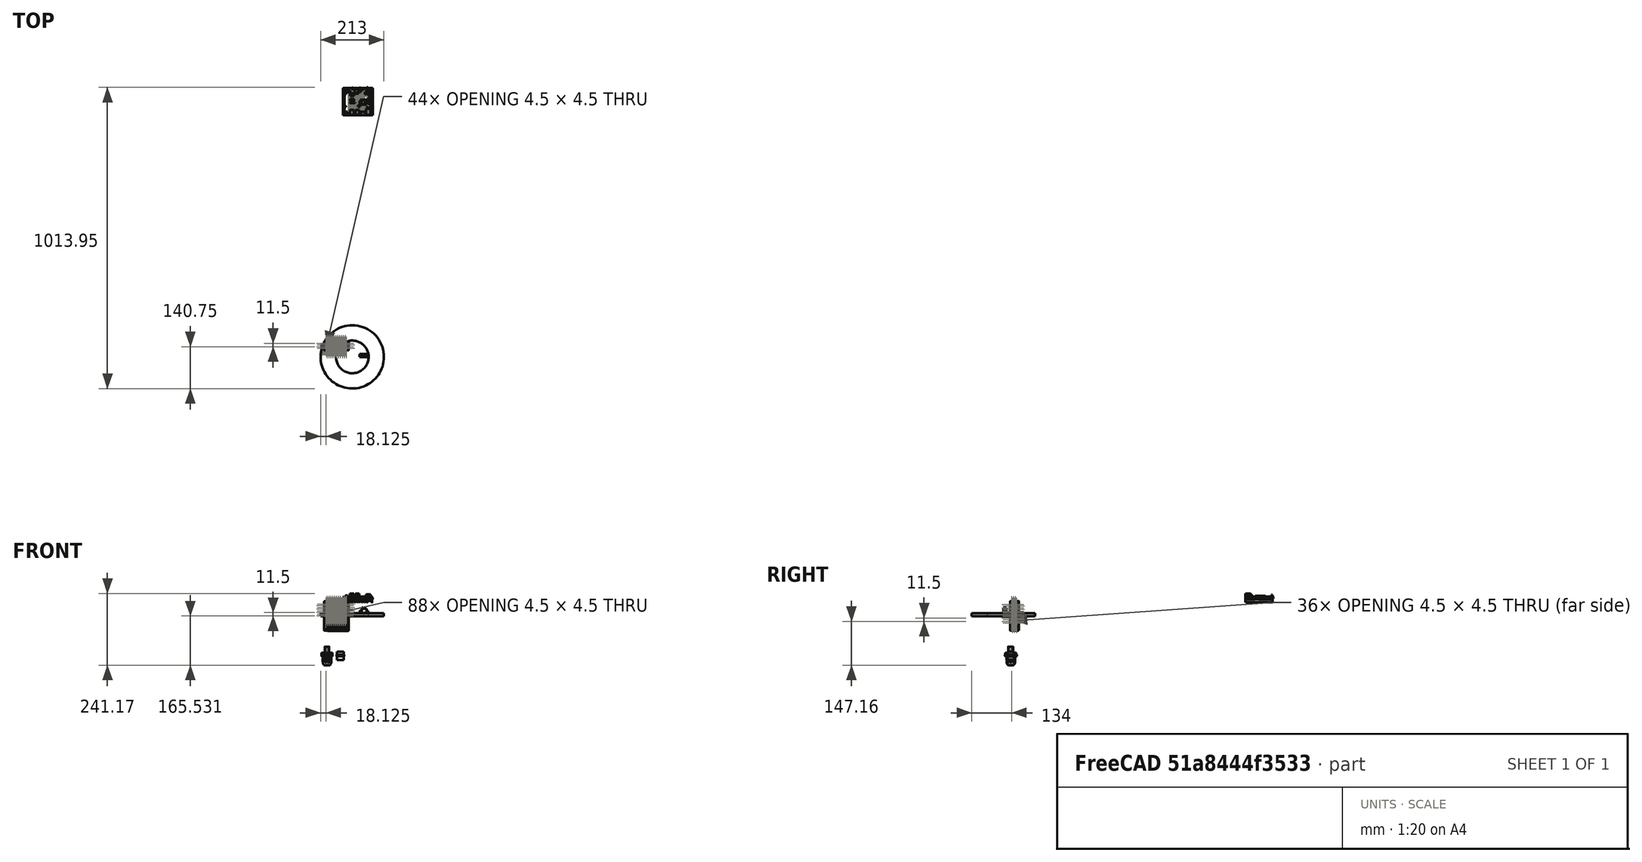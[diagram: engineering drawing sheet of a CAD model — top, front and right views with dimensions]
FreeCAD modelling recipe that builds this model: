
FCSTD DOCUMENT  (FreeCAD 0.20R29410 (Git))
Label: lightSensingModule
License: All rights reserved
LicenseURL: http://en.wikipedia.org/wiki/All_rights_reserved
objects: Part::Feature×21, Part::Cylinder×3, Sketcher::SketchObject×2, Part::Extrusion×2, App::Part×1, Part::MultiFuse×1, Mesh::Feature×1
note: 29 computed .brp shape members not serialized (recipe doc carries the construction recipe); baked Part::Feature solids carry a one-line shape summary decoded from their .brp

FEATURE [Part::Cylinder] Cylinder  label="lens"
  Angle = 360
  AttacherType = Attacher::AttachEngine3D
  FirstAngle = 0
  Height = 10
  Radius = 106.5
  SecondAngle = 0
FEATURE [Part::Cylinder] Cylinder001  label="lens001"
  Angle = 360
  AttacherType = Attacher::AttachEngine3D
  FirstAngle = 0
  Height = 10
  Radius = 55
  SecondAngle = 0
FEATURE [Part::Feature] Part__Feature025  label="CUI_VGS-35C-12"
  Placement = pos=(-55,36,1) rot=(1,0,0;3.14159rad)
  shape: bbox 82.03 x 30.06 x 100 mm, 2215 faces, 10 solids (baked)
FEATURE [Part::Feature] Part__Feature007  label="Heat Sink"
  shape: bbox 100 x 91 x 19 mm, 161 faces (baked)
FEATURE [Part::Feature] Part__Feature008  label="Battery Holder"
  shape: bbox 28.5 x 16 x 6 mm, 91 faces (baked)
FEATURE [Part::Feature] Part__Feature009  label="DC Jack"
  shape: bbox 7.6 x 11.5 x 9.75 mm, 10 faces (baked)
FEATURE [Part::Feature] Part__Feature010  label="PCB"
  shape: bbox 90 x 90 x 3.3 mm, 59 faces (baked)
FEATURE [Part::Feature] Part__Feature011  label="HDMI"
  shape: bbox 14.51 x 11.61 x 5.506 mm, 31 faces (baked)
FEATURE [Part::Feature] Part__Feature012  label="Ethernet"
  shape: bbox 15.9 x 21.4 x 13.5 mm, 25 faces (baked)
FEATURE [Part::Feature] Part__Feature013  label="USB 3.0 B"
  shape: bbox 14.55 x 17.5 x 16.15 mm, 36 faces (baked)
FEATURE [Part::Feature] Part__Feature014  label="USB 3.0 A"
  shape: bbox 14.55 x 17.5 x 16.15 mm, 36 faces (baked)
FEATURE [Part::Feature] Part__Feature015  label="Audio Jack"
  shape: bbox 6.5 x 14 x 4 mm, 10 faces (baked)
FEATURE [Part::Feature] Part__Feature016  label="Fan Plug"
  shape: bbox 3.75 x 7.5 x 4.75 mm, 32 faces (baked)
FEATURE [Part::Feature] Part__Feature017  label="REMOCON"
  shape: bbox 7.006 x 5.006 x 12.01 mm, 30 faces (baked)
FEATURE [Part::Feature] Part__Feature018  label="eMMC"
  shape: bbox 13.5 x 18.5 x 2.8 mm, 33 faces (baked)
FEATURE [Part::Feature] Part__Feature019  label="MicroUSB"
  shape: bbox 7.012 x 4.616 x 3.511 mm, 31 faces (baked)
FEATURE [Part::Feature] Part__Feature020  label="Switch"
  shape: bbox 9 x 5.74 x 3.5 mm, 11 faces (baked)
FEATURE [Part::Feature] Part__Feature021  label="MicroSD Card Socket"
  shape: bbox 11.5 x 5.5 x 3.5 mm, 11 faces (baked)
FEATURE [Part::Feature] Part__Feature022  label="7 Pin Header"
  shape: bbox 17.5 x 2.5 x 8 mm, 41 faces (baked)
FEATURE [Part::Feature] Part__Feature023  label="UART"
  shape: bbox 5 x 12.5 x 6 mm, 43 faces (baked)
FEATURE [Part::Feature] Part__Feature024  label="40 Pin Header"
  shape: bbox 5 x 50 x 8 mm, 206 faces (baked)
FEATURE [App::Part] Odroid_N2__v4  label="Odroid-N2+ v4"
  Group = -> [Part__Feature007,Part__Feature008,Part__Feature009,Part__Feature010,Part__Feature011,Part__Feature012,Part__Feature013,Part__Feature014,Part__Feature015,Part__Feature016,Part__Feature017,Part__Feature018,Part__Feature019,Part__Feature020,Part__Feature021,Part__Feature022,Part__Feature023,Part__Feature024]
  Origin = -> Origin002
  Placement = pos=(31,-814,-44.46) rot=(0,0,1;0rad)
FEATURE [Part::Cylinder] Cylinder002  label="plugIn"
  Angle = 360
  AttacherType = Attacher::AttachEngine3D
  FirstAngle = 0
  Height = 28.19
  Radius = 11
  SecondAngle = 0
FEATURE [Part::Feature] Part__Feature027  label="DCC-RJ6ST-310"
  Placement = pos=(-85,25,-123) rot=(0,0,1;0rad)
  shape: bbox 40.36 x 68.07 x 51.72 mm, 441 faces (baked)
FEATURE [Part::Feature] Part__Feature028  label="DCP-RJ6ST-F"
  Placement = pos=(-85,25,-123.5) rot=(0,1,0;3.14159rad)
  shape: bbox 40.26 x 40.33 x 38.85 mm, 485 faces, 2 solids (baked)
FEATURE [Sketcher::SketchObject] Sketch
  FullyConstrained = true
  sketch-geometry (7):
    g0: LineSegment StartX=12.25 StartY=-7.07254 StartZ=0 EndX=12.25 EndY=7.07254 EndZ=0
    g1: LineSegment StartX=12.25 StartY=7.07254 StartZ=0 EndX=0 EndY=14.1451 EndZ=0
    g2: LineSegment StartX=0 StartY=14.1451 StartZ=0 EndX=-12.25 EndY=7.07254 EndZ=0
    g3: LineSegment StartX=-12.25 StartY=7.07254 StartZ=0 EndX=-12.25 EndY=-7.07254 EndZ=0
    g4: LineSegment StartX=-12.25 StartY=-7.07254 StartZ=0 EndX=0 EndY=-14.1451 EndZ=0
    g5: LineSegment StartX=0 StartY=-14.1451 StartZ=0 EndX=12.25 EndY=-7.07254 EndZ=0
    g6: Circle CenterX=0 CenterY=0 CenterZ=0 NormalX=0 NormalY=0 NormalZ=1 AngleXU=0 Radius=14.1451
  constraints (17):
    c: Coincident(g0,g1)
    c: Coincident(g1,g2)
    c: Coincident(g2,g3)
    c: Coincident(g3,g4)
    c: Coincident(g4,g5)
    c: Coincident(g5,g0)
    c: Equal(g0, g1-g5) x5
    c: PointOnObject(g0,g6)
    c: PointOnObject(g1,g6)
    c: PointOnObject(g2,g6)
    c: PointOnObject(g3,g6)
    c: PointOnObject(g4,g6)
    c: PointOnObject(g5,g6)
    c: DistanceY(g6) = 0
    c: DistanceX(g6) = 0
    c: DistanceX(g1) = 0
    c: DistanceX(g2,g0) = 24.5
FEATURE [Part::Extrusion] Extrude
  Base = -> Sketch
  Dir = (0,0,1)
  DirMode = 2
  FaceMakerClass = Part::FaceMakerBullseye
  LengthFwd = 4.83
  LengthRev = 0
  Placement = pos=(0,0,12.19) rot=(0,0,1;0rad)
  Solid = true
  Symmetric = false
FEATURE [Part::MultiFuse] Fusion  label="powerPlug"
  Placement = pos=(-40,25,-147) rot=(0,0,1;0rad)
  Shapes = -> [Cylinder002,Extrude]
FEATURE [Sketcher::SketchObject] Sketch013
  FullyConstrained = false
  Placement = pos=(0,0,0) rot=(1,0,0;1.5708rad)
  sketch-geometry (884):
    g0: LineSegment StartX=35.7189 StartY=14.4677 StartZ=0 EndX=35.5415 EndY=14.2824 EndZ=0
    g1: LineSegment StartX=35.5415 StartY=14.2079 StartZ=0 EndX=35.4533 EndY=14.1342 EndZ=0
    g2: LineSegment StartX=35.4533 StartY=14.1342 StartZ=0 EndX=35.4583 EndY=14.0618 EndZ=0
    g3: LineSegment StartX=35.4583 StartY=14.0618 StartZ=0 EndX=35.3195 EndY=13.9216 EndZ=0
    g4: LineSegment StartX=35.3195 StartY=13.9216 StartZ=0 EndX=35.3195 EndY=13.853 EndZ=0
    g5: LineSegment StartX=35.3195 StartY=13.853 StartZ=0 EndX=35.248 EndY=13.7975 EndZ=0
    g6: LineSegment StartX=35.248 StartY=13.7975 StartZ=0 EndX=35.248 EndY=13.6573 EndZ=0
    g7: LineSegment StartX=35.248 StartY=13.6573 StartZ=0 EndX=35.1825 EndY=13.5912 EndZ=0
    g8: LineSegment StartX=35.1825 StartY=13.5912 StartZ=0 EndX=35.1825 EndY=13.2647 EndZ=0
    g9: LineSegment StartX=35.1825 StartY=13.2647 StartZ=0 EndX=35.0994 EndY=13.159 EndZ=0
    g10: LineSegment StartX=35.0994 StartY=13.159 StartZ=0 EndX=35.0994 EndY=13.0459 EndZ=0
    g11: LineSegment StartX=35.0994 StartY=13.0459 StartZ=0 EndX=35.0336 EndY=12.9565 EndZ=0
    g12: LineSegment StartX=35.0336 StartY=12.9565 StartZ=0 EndX=35.0336 EndY=12.3489 EndZ=0
    g13: LineSegment StartX=35.0336 StartY=12.3489 StartZ=0 EndX=35.1008 EndY=12.3489 EndZ=0
    g14: LineSegment StartX=35.1008 StartY=12.3489 StartZ=0 EndX=35.1008 EndY=12.2102 EndZ=0
    g15: LineSegment StartX=35.1008 StartY=12.2102 StartZ=0 EndX=35.1709 EndY=12.2072 EndZ=0
    g16: LineSegment StartX=35.1709 StartY=12.2072 StartZ=0 EndX=35.1709 EndY=11.9948 EndZ=0
    g17: LineSegment StartX=35.1709 StartY=11.9948 StartZ=0 EndX=35.2359 EndY=11.9948 EndZ=0
    g18: LineSegment StartX=35.2359 StartY=11.9948 StartZ=0 EndX=35.2359 EndY=11.9181 EndZ=0
    g19: LineSegment StartX=35.2359 StartY=11.9181 StartZ=0 EndX=35.3001 EndY=11.9181 EndZ=0
    g20: LineSegment StartX=35.3001 StartY=11.9181 StartZ=0 EndX=35.3001 EndY=11.8402 EndZ=0
    g21: LineSegment StartX=35.3001 StartY=11.8402 StartZ=0 EndX=35.3675 EndY=11.8402 EndZ=0
    g22: LineSegment StartX=35.3675 StartY=11.8402 StartZ=0 EndX=35.3675 EndY=11.2433 EndZ=0
    g23: LineSegment StartX=35.3675 StartY=11.2433 StartZ=0 EndX=35.435 EndY=11.2433 EndZ=0
    g24: LineSegment StartX=35.435 StartY=11.2433 StartZ=0 EndX=35.435 EndY=11.1727 EndZ=0
    g25: LineSegment StartX=35.435 StartY=11.1727 StartZ=0 EndX=35.5098 EndY=11.1727 EndZ=0
    g26: LineSegment StartX=35.5098 StartY=11.1727 StartZ=0 EndX=35.5098 EndY=11.1026 EndZ=0
    g27: LineSegment StartX=35.5098 StartY=11.1026 StartZ=0 EndX=35.6558 EndY=11.1026 EndZ=0
    g28: LineSegment StartX=35.6558 StartY=11.1026 StartZ=0 EndX=35.6558 EndY=11.0252 EndZ=0
    g29: LineSegment StartX=35.6558 StartY=11.0252 StartZ=0 EndX=35.7128 EndY=11.0252 EndZ=0
    g30: LineSegment StartX=35.7128 StartY=11.0252 StartZ=0 EndX=35.7128 EndY=10.7682 EndZ=0
    g31: LineSegment StartX=35.7128 StartY=10.7682 StartZ=0 EndX=35.7756 EndY=10.7681 EndZ=0
    g32: LineSegment StartX=35.7756 StartY=10.7681 StartZ=0 EndX=35.7756 EndY=10.5644 EndZ=0
    g33: LineSegment StartX=35.7756 StartY=10.5644 StartZ=0 EndX=35.846 EndY=10.5644 EndZ=0
    g34: LineSegment StartX=35.846 StartY=10.5644 StartZ=0 EndX=35.846 EndY=10.4767 EndZ=0
    g35: LineSegment StartX=35.846 StartY=10.4767 StartZ=0 EndX=35.988 EndY=10.4767 EndZ=0
    g36: LineSegment StartX=35.988 StartY=10.4767 StartZ=0 EndX=35.988 EndY=10.4228 EndZ=0
    g37: LineSegment StartX=35.988 StartY=10.4228 StartZ=0 EndX=36.1201 EndY=10.4228 EndZ=0
    g38: LineSegment StartX=36.1201 StartY=10.4228 StartZ=0 EndX=36.1201 EndY=10.2907 EndZ=0
    g39: LineSegment StartX=36.1201 StartY=10.2907 StartZ=0 EndX=36.1926 EndY=10.2907 EndZ=0
    g40: LineSegment StartX=36.1926 StartY=10.2907 StartZ=0 EndX=36.1926 EndY=10.1585 EndZ=0
    g41: LineSegment StartX=36.1926 StartY=10.1585 StartZ=0 EndX=36.2533 EndY=10.1585 EndZ=0
    g42: LineSegment StartX=36.2533 StartY=10.1585 StartZ=0 EndX=36.2533 EndY=10.0897 EndZ=0
    g43: LineSegment StartX=36.2533 StartY=10.0897 StartZ=0 EndX=36.3179 EndY=10.0897 EndZ=0
    g44: LineSegment StartX=36.3179 StartY=10.0897 StartZ=0 EndX=36.3179 EndY=9.8871 EndZ=0
    g45: LineSegment StartX=36.3179 StartY=9.8871 StartZ=0 EndX=36.3888 EndY=9.8871 EndZ=0
    g46: LineSegment StartX=36.3888 StartY=9.8871 StartZ=0 EndX=36.3888 EndY=9.73503 EndZ=0
    g47: LineSegment StartX=36.3888 StartY=9.73503 StartZ=0 EndX=36.4516 EndY=9.73503 EndZ=0
    g48: LineSegment StartX=36.4516 StartY=9.73503 StartZ=0 EndX=36.4516 EndY=9.65617 EndZ=0
    g49: LineSegment StartX=36.4516 StartY=9.65617 StartZ=0 EndX=36.6707 EndY=9.65617 EndZ=0
    g50: LineSegment StartX=36.6707 StartY=9.65617 StartZ=0 EndX=36.6707 EndY=9.58899 EndZ=0
    g51: LineSegment StartX=36.6707 StartY=9.58899 StartZ=0 EndX=36.7335 EndY=9.58899 EndZ=0
    g52: LineSegment StartX=36.7335 StartY=9.58899 StartZ=0 EndX=36.7335 EndY=9.51158 EndZ=0
    g53: LineSegment StartX=36.7335 StartY=9.51158 StartZ=0 EndX=36.7948 EndY=9.51158 EndZ=0
    g54: LineSegment StartX=36.7948 StartY=9.51158 StartZ=0 EndX=36.7948 EndY=9.40351 EndZ=0
    g55: LineSegment StartX=36.7948 StartY=9.40351 StartZ=0 EndX=36.8664 EndY=9.40351 EndZ=0
    g56: LineSegment StartX=36.8664 StartY=9.40351 StartZ=0 EndX=36.8664 EndY=9.2487 EndZ=0
    g57: LineSegment StartX=36.8664 StartY=9.2487 StartZ=0 EndX=36.9292 EndY=9.2487 EndZ=0
    g58: LineSegment StartX=36.9292 StartY=9.2487 StartZ=0 EndX=36.9292 EndY=9.18298 EndZ=0
    g59: LineSegment StartX=36.9292 StartY=9.18298 StartZ=0 EndX=37.0036 EndY=9.18298 EndZ=0
    g60: LineSegment StartX=37.0036 StartY=9.18298 StartZ=0 EndX=37.0036 EndY=9.12121 EndZ=0
    g61: LineSegment StartX=37.0036 StartY=9.12121 StartZ=0 EndX=37.066 EndY=9.12121 EndZ=0
    g62: LineSegment StartX=37.066 StartY=9.12121 StartZ=0 EndX=37.066 EndY=8.98122 EndZ=0
    g63: LineSegment StartX=37.066 StartY=8.98122 StartZ=0 EndX=37.1365 EndY=8.98122 EndZ=0
    g64: LineSegment StartX=37.1365 StartY=8.98122 StartZ=0 EndX=37.1365 EndY=8.85617 EndZ=0
    g65: LineSegment StartX=37.1365 StartY=8.85617 StartZ=0 EndX=37.2117 EndY=8.85617 EndZ=0
    g66: LineSegment StartX=37.2117 StartY=8.85617 StartZ=0 EndX=37.2117 EndY=8.77808 EndZ=0
    g67: LineSegment StartX=37.2117 StartY=8.77808 StartZ=0 EndX=37.276 EndY=8.7779 EndZ=0
    g68: LineSegment StartX=37.276 StartY=8.7779 StartZ=0 EndX=37.276 EndY=8.70839 EndZ=0
    g69: LineSegment StartX=37.276 StartY=8.70839 StartZ=0 EndX=37.3475 EndY=8.70839 EndZ=0
    g70: LineSegment StartX=37.3475 StartY=8.70839 StartZ=0 EndX=37.3475 EndY=8.58602 EndZ=0
    g71: LineSegment StartX=37.3475 StartY=8.58602 StartZ=0 EndX=37.4111 EndY=8.58602 EndZ=0
    g72: LineSegment StartX=37.4111 StartY=8.58602 StartZ=0 EndX=37.4111 EndY=8.50272 EndZ=0
    g73: LineSegment StartX=37.4111 StartY=8.50272 StartZ=0 EndX=37.4778 EndY=8.50272 EndZ=0
    g74: LineSegment StartX=37.4778 StartY=8.50272 StartZ=0 EndX=37.4778 EndY=8.37852 EndZ=0
    g75: LineSegment StartX=37.4778 StartY=8.37852 StartZ=0 EndX=37.55 EndY=8.37852 EndZ=0
    g76: LineSegment StartX=37.55 StartY=8.37852 StartZ=0 EndX=37.55 EndY=8.29594 EndZ=0
    g77: LineSegment StartX=37.55 StartY=8.29594 StartZ=0 EndX=37.6238 EndY=8.29594 EndZ=0
    g78: LineSegment StartX=37.6238 StartY=8.29594 StartZ=0 EndX=37.6238 EndY=8.20831 EndZ=0
    g79: LineSegment StartX=37.6238 StartY=8.20831 StartZ=0 EndX=37.6953 EndY=8.21123 EndZ=0
    g80: LineSegment StartX=37.6953 StartY=8.21123 StartZ=0 EndX=37.6953 EndY=8.14022 EndZ=0
    g81: LineSegment StartX=37.6953 StartY=8.14022 StartZ=0 EndX=37.7536 EndY=8.14414 EndZ=0
    g82: LineSegment StartX=37.7536 StartY=8.14414 StartZ=0 EndX=37.7574 EndY=8.06459 EndZ=0
    g83: LineSegment StartX=37.7574 StartY=8.06459 StartZ=0 EndX=37.8181 EndY=8.06459 EndZ=0
    g84: LineSegment StartX=37.8181 StartY=8.06459 StartZ=0 EndX=37.8216 EndY=7.98967 EndZ=0
    g85: LineSegment StartX=37.8216 StartY=7.98967 StartZ=0 EndX=38.1025 EndY=7.98967 EndZ=0
    g86: LineSegment StartX=38.1025 StartY=7.98967 StartZ=0 EndX=38.1917 EndY=8.08042 EndZ=0
    g87: LineSegment StartX=38.1917 StartY=8.08042 StartZ=0 EndX=38.2417 EndY=8.08577 EndZ=0
    g88: LineSegment StartX=38.2417 StartY=8.08577 StartZ=0 EndX=38.4557 EndY=8.32302 EndZ=0
    g89: LineSegment StartX=38.4557 StartY=8.32302 StartZ=0 EndX=38.5235 EndY=8.32302 EndZ=0
    g90: LineSegment StartX=38.5235 StartY=8.32302 StartZ=0 EndX=38.5887 EndY=8.40314 EndZ=0
    g91: LineSegment StartX=38.5887 StartY=8.40314 StartZ=0 EndX=38.6773 EndY=8.40314 EndZ=0
    g92: LineSegment StartX=38.6773 StartY=8.40314 StartZ=0 EndX=39.0643 EndY=8.80818 EndZ=0
    g93: LineSegment StartX=39.0643 StartY=8.80818 StartZ=0 EndX=39.152 EndY=8.80818 EndZ=0
    g94: LineSegment StartX=39.152 StartY=8.80818 StartZ=0 EndX=39.5355 EndY=9.19803 EndZ=0
    g95: LineSegment StartX=39.5355 StartY=9.19803 StartZ=0 EndX=39.6318 EndY=9.19803 EndZ=0
    g96: LineSegment StartX=39.6318 StartY=9.19803 StartZ=0 EndX=39.792 EndY=9.38195 EndZ=0
    g97: LineSegment StartX=39.792 StartY=9.38195 StartZ=0 EndX=39.7884 EndY=9.45608 EndZ=0
    g98: LineSegment StartX=39.7884 StartY=9.45608 StartZ=0 EndX=39.9772 EndY=9.63446 EndZ=0
    g99: LineSegment StartX=39.9772 StartY=9.63446 StartZ=0 EndX=39.9772 EndY=9.72533 EndZ=0
    g100: LineSegment StartX=39.9772 StartY=9.72533 StartZ=0 EndX=40.1697 EndY=9.91904 EndZ=0
    g101: LineSegment StartX=40.1697 StartY=9.91904 StartZ=0 EndX=40.1746 EndY=9.99558 EndZ=0
    g102: LineSegment StartX=40.1746 StartY=9.99558 StartZ=0 EndX=40.2388 EndY=10.0603 EndZ=0
    g103: LineSegment StartX=40.2388 StartY=10.0603 StartZ=0 EndX=40.2423 EndY=10.1261 EndZ=0
    g104: LineSegment StartX=40.2423 StartY=10.1261 StartZ=0 EndX=40.5948 EndY=10.4793 EndZ=0
    g105: LineSegment StartX=40.5948 StartY=10.4793 StartZ=0 EndX=40.5948 EndY=10.5499 EndZ=0
    g106: LineSegment StartX=40.5948 StartY=10.5499 StartZ=0 EndX=40.6701 EndY=10.618 EndZ=0
    g107: LineSegment StartX=40.6701 StartY=10.618 StartZ=0 EndX=40.6581 EndY=10.6527 EndZ=0
    g108: LineSegment StartX=40.6581 StartY=10.6527 StartZ=0 EndX=40.6988 EndY=10.6527 EndZ=0
    g109: LineSegment StartX=40.6988 StartY=10.6527 StartZ=0 EndX=40.9317 EndY=10.8877 EndZ=0
    g110: LineSegment StartX=40.9317 StartY=10.8877 StartZ=0 EndX=40.9317 EndY=10.9592 EndZ=0
    g111: LineSegment StartX=40.9317 StartY=10.9592 StartZ=0 EndX=41.0136 EndY=11.0405 EndZ=0
    g112: LineSegment StartX=41.0136 StartY=11.0405 StartZ=0 EndX=41.0068 EndY=11.1648 EndZ=0
    g113: LineSegment StartX=41.0068 StartY=11.1648 StartZ=0 EndX=41.0763 EndY=11.2275 EndZ=0
    g114: LineSegment StartX=41.0763 StartY=11.2275 StartZ=0 EndX=41.0723 EndY=11.2979 EndZ=0
    g115: LineSegment StartX=41.0723 StartY=11.2979 StartZ=0 EndX=41.15 EndY=11.3821 EndZ=0
    g116: LineSegment StartX=41.15 StartY=11.3821 StartZ=0 EndX=41.15 EndY=11.5724 EndZ=0
    g117: LineSegment StartX=41.15 StartY=11.5724 StartZ=0 EndX=41.2317 EndY=11.6351 EndZ=0
    g118: LineSegment StartX=41.2317 StartY=11.6351 StartZ=0 EndX=41.2155 EndY=11.7717 EndZ=0
    g119: LineSegment StartX=41.2155 StartY=11.7717 StartZ=0 EndX=41.2837 EndY=11.8432 EndZ=0
    g120: LineSegment StartX=41.2837 StartY=11.8432 StartZ=0 EndX=41.2786 EndY=11.8698 EndZ=0
    g121: LineSegment StartX=41.2786 StartY=11.8698 StartZ=0 EndX=41.3138 EndY=11.8698 EndZ=0
    g122: LineSegment StartX=41.3138 StartY=11.8698 StartZ=0 EndX=41.5455 EndY=12.1045 EndZ=0
    g123: LineSegment StartX=41.5455 StartY=12.1045 StartZ=0 EndX=41.5618 EndY=12.4305 EndZ=0
    g124: LineSegment StartX=41.5618 StartY=12.4305 StartZ=0 EndX=41.6277 EndY=12.505 EndZ=0
    g125: LineSegment StartX=41.6277 StartY=12.505 StartZ=0 EndX=41.6277 EndY=12.6108 EndZ=0
    g126: LineSegment StartX=41.6277 StartY=12.6108 StartZ=0 EndX=41.692 EndY=12.5393 EndZ=0
    g127: LineSegment StartX=41.692 StartY=12.5393 StartZ=0 EndX=41.7679 EndY=12.5393 EndZ=0
    g128: LineSegment StartX=41.7679 StartY=12.5393 StartZ=0 EndX=41.7679 EndY=12.4516 EndZ=0
    g129: LineSegment StartX=41.7679 StartY=12.4516 StartZ=0 EndX=41.8336 EndY=12.4546 EndZ=0
    g130: LineSegment StartX=41.8336 StartY=12.4546 StartZ=0 EndX=41.8336 EndY=12.3903 EndZ=0
    g131: LineSegment StartX=41.8336 StartY=12.3903 StartZ=0 EndX=41.8935 EndY=12.3903 EndZ=0
    g132: LineSegment StartX=41.8935 StartY=12.3903 StartZ=0 EndX=41.8935 EndY=12.3173 EndZ=0
    g133: LineSegment StartX=41.8935 StartY=12.3173 StartZ=0 EndX=41.9592 EndY=12.3217 EndZ=0
    g134: LineSegment StartX=41.9592 StartY=12.3217 StartZ=0 EndX=41.9651 EndY=12.2501 EndZ=0
    g135: LineSegment StartX=41.9651 StartY=12.2501 StartZ=0 EndX=42.0235 EndY=12.2559 EndZ=0
    g136: LineSegment StartX=42.0235 StartY=12.2559 StartZ=0 EndX=42.0264 EndY=12.1829 EndZ=0
    g137: LineSegment StartX=42.0264 StartY=12.1829 StartZ=0 EndX=42.1067 EndY=12.1888 EndZ=0
    g138: LineSegment StartX=42.1067 StartY=12.1888 StartZ=0 EndX=42.1067 EndY=12.1143 EndZ=0
    g139: LineSegment StartX=42.1067 StartY=12.1143 StartZ=0 EndX=42.2426 EndY=12.1216 EndZ=0
    g140: LineSegment StartX=42.2426 StartY=12.1216 StartZ=0 EndX=42.2426 EndY=12.0413 EndZ=0
    g141: LineSegment StartX=42.2426 StartY=12.0413 StartZ=0 EndX=42.4427 EndY=12.0413 EndZ=0
    g142: LineSegment StartX=42.4427 StartY=12.0413 StartZ=0 EndX=42.45 EndY=11.9566 EndZ=0
    g143: LineSegment StartX=42.45 StartY=11.9566 StartZ=0 EndX=42.523 EndY=11.9639 EndZ=0
    g144: LineSegment StartX=42.523 StartY=11.9639 StartZ=0 EndX=42.5274 EndY=11.8952 EndZ=0
    g145: LineSegment StartX=42.5274 StartY=11.8952 StartZ=0 EndX=42.5931 EndY=11.9011 EndZ=0
    g146: LineSegment StartX=42.5931 StartY=11.9011 StartZ=0 EndX=42.5931 EndY=11.847 EndZ=0
    g147: LineSegment StartX=42.5931 StartY=11.847 StartZ=0 EndX=42.6457 EndY=11.8499 EndZ=0
    g148: LineSegment StartX=42.6457 StartY=11.8499 StartZ=0 EndX=42.6457 EndY=11.7886 EndZ=0
    g149: LineSegment StartX=42.6457 StartY=11.7886 StartZ=0 EndX=42.7844 EndY=11.7886 EndZ=0
    g150: LineSegment StartX=42.7844 StartY=11.7886 StartZ=0 EndX=42.7844 EndY=11.7131 EndZ=0
    g151: LineSegment StartX=42.7844 StartY=11.7131 StartZ=0 EndX=43.0642 EndY=11.7131 EndZ=0
    g152: LineSegment StartX=43.0642 StartY=11.7131 StartZ=0 EndX=43.0642 EndY=11.6357 EndZ=0
    g153: LineSegment StartX=43.0642 StartY=11.6357 StartZ=0 EndX=43.1985 EndY=11.6357 EndZ=0
    g154: LineSegment StartX=43.1985 StartY=11.6357 StartZ=0 EndX=43.1985 EndY=11.5714 EndZ=0
    g155: LineSegment StartX=43.1985 StartY=11.5714 StartZ=0 EndX=43.2613 EndY=11.5714 EndZ=0
    g156: LineSegment StartX=43.2613 StartY=11.5714 StartZ=0 EndX=43.2613 EndY=11.5086 EndZ=0
    g157: LineSegment StartX=43.2613 StartY=11.5086 StartZ=0 EndX=43.3285 EndY=11.5086 EndZ=0
    g158: LineSegment StartX=43.3285 StartY=11.5086 StartZ=0 EndX=43.3285 EndY=11.4327 EndZ=0
    g159: LineSegment StartX=43.3285 StartY=11.4327 StartZ=0 EndX=43.3913 EndY=11.4371 EndZ=0
    g160: LineSegment StartX=43.3913 StartY=11.4371 StartZ=0 EndX=43.3932 EndY=11.3717 EndZ=0
    g161: LineSegment StartX=43.3932 StartY=11.3717 StartZ=0 EndX=43.7436 EndY=11.3717 EndZ=0
    g162: LineSegment StartX=43.7436 StartY=11.3717 StartZ=0 EndX=43.7436 EndY=11.3021 EndZ=0
    g163: LineSegment StartX=43.7436 StartY=11.3021 StartZ=0 EndX=43.8098 EndY=11.3021 EndZ=0
    g164: LineSegment StartX=43.8098 StartY=11.3021 StartZ=0 EndX=43.8134 EndY=11.2285 EndZ=0
    g165: LineSegment StartX=43.8134 StartY=11.2285 StartZ=0 EndX=44.0238 EndY=11.2285 EndZ=0
    g166: LineSegment StartX=44.0238 StartY=11.2285 StartZ=0 EndX=44.0238 EndY=11.1603 EndZ=0
    g167: LineSegment StartX=44.0238 StartY=11.1603 StartZ=0 EndX=44.1542 EndY=11.1603 EndZ=0
    g168: LineSegment StartX=44.1542 StartY=11.1603 StartZ=0 EndX=44.1506 EndY=11.0922 EndZ=0
    g169: LineSegment StartX=44.1506 StartY=11.0922 StartZ=0 EndX=44.2845 EndY=11.1005 EndZ=0
    g170: LineSegment StartX=44.2845 StartY=11.1005 StartZ=0 EndX=44.2845 EndY=11.0276 EndZ=0
    g171: LineSegment StartX=44.2845 StartY=11.0276 StartZ=0 EndX=44.3538 EndY=11.0312 EndZ=0
    g172: LineSegment StartX=44.3538 StartY=11.0312 StartZ=0 EndX=44.3538 EndY=10.9534 EndZ=0
    g173: LineSegment StartX=44.3538 StartY=10.9534 StartZ=0 EndX=44.4925 EndY=10.9534 EndZ=0
    g174: LineSegment StartX=44.4925 StartY=10.9534 StartZ=0 EndX=44.4925 EndY=10.9066 EndZ=0
    g175: LineSegment StartX=44.4925 StartY=10.9066 StartZ=0 EndX=44.8405 EndY=10.9066 EndZ=0
    g176: LineSegment StartX=44.8405 StartY=10.9066 StartZ=0 EndX=44.8405 EndY=10.8227 EndZ=0
    g177: LineSegment StartX=44.8405 StartY=10.8227 StartZ=0 EndX=44.9671 EndY=10.8245 EndZ=0
    g178: LineSegment StartX=44.9671 StartY=10.8245 StartZ=0 EndX=44.9671 EndY=10.7496 EndZ=0
    g179: LineSegment StartX=44.9671 StartY=10.7496 StartZ=0 EndX=45.2382 EndY=10.7496 EndZ=0
    g180: LineSegment StartX=45.2382 StartY=10.7496 StartZ=0 EndX=45.2382 EndY=10.6783 EndZ=0
    g181: LineSegment StartX=45.2382 StartY=10.6783 StartZ=0 EndX=45.438 EndY=10.6783 EndZ=0
    g182: LineSegment StartX=45.438 StartY=10.6783 StartZ=0 EndX=45.438 EndY=10.6176 EndZ=0
    g183: LineSegment StartX=45.438 StartY=10.6176 StartZ=0 EndX=45.8572 EndY=10.6176 EndZ=0
    g184: LineSegment StartX=45.8572 StartY=10.6176 StartZ=0 EndX=45.8572 EndY=10.548 EndZ=0
    g185: LineSegment StartX=45.8572 StartY=10.548 StartZ=0 EndX=46.2711 EndY=10.548 EndZ=0
    g186: LineSegment StartX=46.2711 StartY=10.548 StartZ=0 EndX=46.5712 EndY=10.876 EndZ=0
    g187: LineSegment StartX=46.5712 StartY=10.876 StartZ=0 EndX=46.568 EndY=10.9537 EndZ=0
    g188: LineSegment StartX=46.568 StartY=10.9537 StartZ=0 EndX=46.6513 EndY=11.0387 EndZ=0
    g189: LineSegment StartX=46.6513 StartY=11.0387 StartZ=0 EndX=46.6513 EndY=11.2162 EndZ=0
    g190: LineSegment StartX=46.6513 StartY=11.2162 StartZ=0 EndX=46.7535 EndY=11.317 EndZ=0
    g191: LineSegment StartX=46.7535 StartY=11.317 StartZ=0 EndX=46.7462 EndY=11.4353 EndZ=0
    g192: LineSegment StartX=46.7462 StartY=11.4353 StartZ=0 EndX=46.8178 EndY=11.5141 EndZ=0
    g193: LineSegment StartX=46.8178 StartY=11.5141 StartZ=0 EndX=46.8081 EndY=11.636 EndZ=0
    g194: LineSegment StartX=46.8081 StartY=11.636 StartZ=0 EndX=46.8919 EndY=11.7287 EndZ=0
    g195: LineSegment StartX=46.8919 StartY=11.7287 StartZ=0 EndX=46.8919 EndY=11.9142 EndZ=0
    g196: LineSegment StartX=46.8919 StartY=11.9142 StartZ=0 EndX=46.9704 EndY=12.0106 EndZ=0
    g197: LineSegment StartX=46.9704 StartY=12.0106 StartZ=0 EndX=46.9704 EndY=13.0147 EndZ=0
    g198: LineSegment StartX=46.9704 StartY=13.0147 StartZ=0 EndX=47.1435 EndY=13.1957 EndZ=0
    g199: LineSegment StartX=47.1435 StartY=13.1957 StartZ=0 EndX=47.1435 EndY=13.5812 EndZ=0
    g200: LineSegment StartX=47.1435 StartY=13.5812 StartZ=0 EndX=47.0232 EndY=13.5812 EndZ=0
    g201: LineSegment StartX=47.0232 StartY=13.5812 StartZ=0 EndX=47.0232 EndY=13.968 EndZ=0
    g202: LineSegment StartX=47.0232 StartY=13.968 StartZ=0 EndX=46.9387 EndY=13.981 EndZ=0
    g203: LineSegment StartX=46.9387 StartY=13.981 StartZ=0 EndX=46.9387 EndY=14.1923 EndZ=0
    g204: LineSegment StartX=46.9387 StartY=14.1923 StartZ=0 EndX=46.8607 EndY=14.189 EndZ=0
    g205: LineSegment StartX=46.8607 StartY=14.189 StartZ=0 EndX=46.8607 EndY=14.2768 EndZ=0
    g206: LineSegment StartX=46.8607 StartY=14.2768 StartZ=0 EndX=46.9745 EndY=14.4003 EndZ=0
    g207: LineSegment StartX=46.9745 StartY=14.4003 StartZ=0 EndX=46.9842 EndY=14.6473 EndZ=0
    g208: LineSegment StartX=46.9842 StartY=14.6473 StartZ=0 EndX=46.8672 EndY=14.6603 EndZ=0
    g209: LineSegment StartX=46.8672 StartY=14.6603 StartZ=0 EndX=46.8672 EndY=14.8066 EndZ=0
    g210: LineSegment StartX=46.8672 StartY=14.8066 StartZ=0 EndX=46.799 EndY=14.8131 EndZ=0
    g211: LineSegment StartX=46.799 StartY=14.8131 StartZ=0 EndX=46.7957 EndY=14.8846 EndZ=0
    g212: LineSegment StartX=46.7957 StartY=14.8846 StartZ=0 EndX=46.7372 EndY=14.8911 EndZ=0
    g213: LineSegment StartX=46.7372 StartY=14.8911 StartZ=0 EndX=46.7502 EndY=15.0699 EndZ=0
    g214: LineSegment StartX=46.7502 StartY=15.0699 StartZ=0 EndX=46.6592 EndY=15.0764 EndZ=0
    g215: LineSegment StartX=46.6592 StartY=15.0764 StartZ=0 EndX=46.6592 EndY=15.2096 EndZ=0
    g216: LineSegment StartX=46.6592 StartY=15.2096 StartZ=0 EndX=46.7535 EndY=15.2811 EndZ=0
    g217: LineSegment StartX=46.7535 StartY=15.2811 StartZ=0 EndX=47.5498 EndY=15.2811 EndZ=0
    g218: LineSegment StartX=47.5498 StartY=15.2811 StartZ=0 EndX=47.5498 EndY=15.2015 EndZ=0
    g219: LineSegment StartX=47.5498 StartY=15.2015 StartZ=0 EndX=48.1326 EndY=15.2015 EndZ=0
    g220: LineSegment StartX=48.1326 StartY=15.2015 StartZ=0 EndX=48.1915 EndY=15.2887 EndZ=0
    g221: LineSegment StartX=48.1915 StartY=15.2887 StartZ=0 EndX=48.2811 EndY=15.2887 EndZ=0
    g222: LineSegment StartX=48.2811 StartY=15.2887 StartZ=0 EndX=48.4046 EndY=15.4194 EndZ=0
    g223: LineSegment StartX=48.4046 StartY=15.4194 StartZ=0 EndX=48.6512 EndY=15.4194 EndZ=0
    g224: LineSegment StartX=48.6512 StartY=15.4194 StartZ=0 EndX=48.6512 EndY=15.3322 EndZ=0
    g225: LineSegment StartX=48.6512 StartY=15.3322 StartZ=0 EndX=48.9084 EndY=15.3322 EndZ=0
    g226: LineSegment StartX=48.9084 StartY=15.3322 StartZ=0 EndX=48.9084 EndY=15.2647 EndZ=0
    g227: LineSegment StartX=48.9084 StartY=15.2647 StartZ=0 EndX=49.1131 EndY=15.2647 EndZ=0
    g228: LineSegment StartX=49.1131 StartY=15.2647 StartZ=0 EndX=49.1131 EndY=15.171 EndZ=0
    g229: LineSegment StartX=49.1131 StartY=15.171 StartZ=0 EndX=49.344 EndY=15.171 EndZ=0
    g230: LineSegment StartX=49.344 StartY=15.171 StartZ=0 EndX=49.4317 EndY=15.2779 EndZ=0
    g231: LineSegment StartX=49.4317 StartY=15.2779 StartZ=0 EndX=49.513 EndY=15.2714 EndZ=0
    g232: LineSegment StartX=49.513 StartY=15.2714 StartZ=0 EndX=49.6365 EndY=15.4177 EndZ=0
    g233: LineSegment StartX=49.6365 StartY=15.4177 StartZ=0 EndX=51.1609 EndY=15.4177 EndZ=0
    g234: LineSegment StartX=51.1609 StartY=15.4177 StartZ=0 EndX=51.2713 EndY=15.4747 EndZ=0
    g235: LineSegment StartX=51.2713 StartY=15.4747 StartZ=0 EndX=51.8707 EndY=15.4747 EndZ=0
    g236: LineSegment StartX=51.8707 StartY=15.4747 StartZ=0 EndX=51.9501 EndY=15.5501 EndZ=0
    g237: LineSegment StartX=51.9501 StartY=15.5501 StartZ=0 EndX=52.0613 EndY=15.5501 EndZ=0
    g238: LineSegment StartX=52.0613 StartY=15.5501 StartZ=0 EndX=52.1566 EndY=15.6335 EndZ=0
    g239: LineSegment StartX=52.1566 StartY=15.6335 StartZ=0 EndX=53.0776 EndY=15.6335 EndZ=0
    g240: LineSegment StartX=53.0776 StartY=15.6335 StartZ=0 EndX=53.2557 EndY=15.8082 EndZ=0
    g241: LineSegment StartX=53.2557 StartY=15.8082 StartZ=0 EndX=53.2557 EndY=16.103 EndZ=0
    g242: LineSegment StartX=53.2557 StartY=16.103 StartZ=0 EndX=53.1958 EndY=16.103 EndZ=0
    g243: LineSegment StartX=53.1958 StartY=16.103 StartZ=0 EndX=53.1958 EndY=16.3046 EndZ=0
    g244: LineSegment StartX=53.1958 StartY=16.3046 StartZ=0 EndX=53.1301 EndY=16.3017 EndZ=0
    g245: LineSegment StartX=53.1301 StartY=16.3017 StartZ=0 EndX=53.1301 EndY=16.4404 EndZ=0
    g246: LineSegment StartX=53.1301 StartY=16.4404 StartZ=0 EndX=53.0594 EndY=16.4404 EndZ=0
    g247: LineSegment StartX=53.0594 StartY=16.4404 StartZ=0 EndX=53.0558 EndY=16.5171 EndZ=0
    g248: LineSegment StartX=53.0558 StartY=16.5171 StartZ=0 EndX=52.9773 EndY=16.5171 EndZ=0
    g249: LineSegment StartX=52.9773 StartY=16.5171 StartZ=0 EndX=52.9773 EndY=16.6455 EndZ=0
    g250: LineSegment StartX=52.9773 StartY=16.6455 StartZ=0 EndX=52.9219 EndY=16.6452 EndZ=0
    g251: LineSegment StartX=52.9219 StartY=16.6452 StartZ=0 EndX=52.9219 EndY=16.7146 EndZ=0
    g252: LineSegment StartX=52.9219 StartY=16.7146 StartZ=0 EndX=52.8549 EndY=16.7146 EndZ=0
    g253: LineSegment StartX=52.8549 StartY=16.7146 StartZ=0 EndX=52.8535 EndY=16.7863 EndZ=0
    g254: LineSegment StartX=52.8535 StartY=16.7863 StartZ=0 EndX=52.7868 EndY=16.7863 EndZ=0
    g255: LineSegment StartX=52.7868 StartY=16.7863 StartZ=0 EndX=52.7868 EndY=16.9211 EndZ=0
    g256: LineSegment StartX=52.7868 StartY=16.9211 StartZ=0 EndX=52.715 EndY=16.9211 EndZ=0
    g257: LineSegment StartX=52.715 StartY=16.9211 StartZ=0 EndX=52.715 EndY=16.98 EndZ=0
    g258: LineSegment StartX=52.715 StartY=16.98 StartZ=0 EndX=52.6457 EndY=16.98 EndZ=0
    g259: LineSegment StartX=52.6457 StartY=16.98 StartZ=0 EndX=52.6457 EndY=17.0366 EndZ=0
    g260: LineSegment StartX=52.6457 StartY=17.0366 StartZ=0 EndX=52.5763 EndY=17.0366 EndZ=0
    g261: LineSegment StartX=52.5763 StartY=17.0366 StartZ=0 EndX=52.5763 EndY=17.128 EndZ=0
    g262: LineSegment StartX=52.5763 StartY=17.128 StartZ=0 EndX=52.5147 EndY=17.128 EndZ=0
    g263: LineSegment StartX=52.5147 StartY=17.128 StartZ=0 EndX=52.5147 EndY=17.2695 EndZ=0
    g264: LineSegment StartX=52.5147 StartY=17.2695 StartZ=0 EndX=52.4502 EndY=17.2647 EndZ=0
    g265: LineSegment StartX=52.4502 StartY=17.2647 StartZ=0 EndX=52.4454 EndY=17.336 EndZ=0
    g266: LineSegment StartX=52.4454 StartY=17.336 StartZ=0 EndX=52.3797 EndY=17.3384 EndZ=0
    g267: LineSegment StartX=52.3797 StartY=17.3384 StartZ=0 EndX=52.3829 EndY=17.4058 EndZ=0
    g268: LineSegment StartX=52.3829 StartY=17.4058 StartZ=0 EndX=52.318 EndY=17.4026 EndZ=0
    g269: LineSegment StartX=52.318 StartY=17.4026 StartZ=0 EndX=52.318 EndY=17.4715 EndZ=0
    g270: LineSegment StartX=52.318 StartY=17.4715 StartZ=0 EndX=52.2451 EndY=17.4715 EndZ=0
    g271: LineSegment StartX=52.2451 StartY=17.4715 StartZ=0 EndX=52.2451 EndY=17.5364 EndZ=0
    g272: LineSegment StartX=52.2451 StartY=17.5364 StartZ=0 EndX=52.1833 EndY=17.5388 EndZ=0
    g273: LineSegment StartX=52.1833 StartY=17.5388 StartZ=0 EndX=52.1833 EndY=17.6077 EndZ=0
    g274: LineSegment StartX=52.1833 StartY=17.6077 StartZ=0 EndX=52.1144 EndY=17.6077 EndZ=0
    g275: LineSegment StartX=52.1144 StartY=17.6077 StartZ=0 EndX=52.1144 EndY=17.6741 EndZ=0
    g276: LineSegment StartX=52.1144 StartY=17.6741 StartZ=0 EndX=52.0495 EndY=17.6741 EndZ=0
    g277: LineSegment StartX=52.0495 StartY=17.6741 StartZ=0 EndX=52.0495 EndY=17.7495 EndZ=0
    g278: LineSegment StartX=52.0495 StartY=17.7495 StartZ=0 EndX=51.9017 EndY=17.7495 EndZ=0
    g279: LineSegment StartX=51.9017 StartY=17.7495 StartZ=0 EndX=51.9017 EndY=17.8092 EndZ=0
    g280: LineSegment StartX=51.9017 StartY=17.8092 StartZ=0 EndX=51.8351 EndY=17.8092 EndZ=0
    g281: LineSegment StartX=51.8351 StartY=17.8092 StartZ=0 EndX=51.8351 EndY=17.8911 EndZ=0
    g282: LineSegment StartX=51.8351 StartY=17.8911 StartZ=0 EndX=51.7639 EndY=17.8911 EndZ=0
    g283: LineSegment StartX=51.7639 StartY=17.8911 StartZ=0 EndX=51.7639 EndY=17.9626 EndZ=0
    g284: LineSegment StartX=51.7639 StartY=17.9626 StartZ=0 EndX=51.6325 EndY=17.9626 EndZ=0
    g285: LineSegment StartX=51.6325 StartY=17.9626 StartZ=0 EndX=51.6325 EndY=18.0284 EndZ=0
    g286: LineSegment StartX=51.6325 StartY=18.0284 StartZ=0 EndX=51.485 EndY=18.0284 EndZ=0
    g287: LineSegment StartX=51.485 StartY=18.0284 StartZ=0 EndX=51.485 EndY=18.0711 EndZ=0
    g288: LineSegment StartX=51.485 StartY=18.0711 StartZ=0 EndX=51.4163 EndY=18.0711 EndZ=0
    g289: LineSegment StartX=51.4163 StartY=18.0711 StartZ=0 EndX=51.4163 EndY=18.1587 EndZ=0
    g290: LineSegment StartX=51.4163 StartY=18.1587 StartZ=0 EndX=51.2878 EndY=18.1587 EndZ=0
    g291: LineSegment StartX=51.2878 StartY=18.1587 StartZ=0 EndX=51.2878 EndY=18.2275 EndZ=0
    g292: LineSegment StartX=51.2878 StartY=18.2275 StartZ=0 EndX=51.2232 EndY=18.2275 EndZ=0
    g293: LineSegment StartX=51.2232 StartY=18.2275 StartZ=0 EndX=51.2267 EndY=18.2921 EndZ=0
    g294: LineSegment StartX=51.2267 StartY=18.2921 StartZ=0 EndX=51.1526 EndY=18.2921 EndZ=0
    g295: LineSegment StartX=51.1526 StartY=18.2921 StartZ=0 EndX=51.1526 EndY=18.3662 EndZ=0
    g296: LineSegment StartX=51.1526 StartY=18.3662 StartZ=0 EndX=51.0845 EndY=18.3602 EndZ=0
    g297: LineSegment StartX=51.0845 StartY=18.3602 StartZ=0 EndX=51.0845 EndY=18.4424 EndZ=0
    g298: LineSegment StartX=51.0845 StartY=18.4424 StartZ=0 EndX=51.0222 EndY=18.4424 EndZ=0
    g299: LineSegment StartX=51.0222 StartY=18.4424 StartZ=0 EndX=51.0222 EndY=18.5138 EndZ=0
    g300: LineSegment StartX=51.0222 StartY=18.5138 StartZ=0 EndX=50.8169 EndY=18.5138 EndZ=0
    g301: LineSegment StartX=50.8169 StartY=18.5138 StartZ=0 EndX=50.7878 EndY=18.6026 EndZ=0
    g302: LineSegment StartX=50.7878 StartY=18.6026 StartZ=0 EndX=50.7494 EndY=18.6113 EndZ=0
    g303: LineSegment StartX=50.7494 StartY=18.6113 StartZ=0 EndX=50.7397 EndY=18.6731 EndZ=0
    g304: LineSegment StartX=50.7397 StartY=18.6731 StartZ=0 EndX=50.5414 EndY=18.6536 EndZ=0
    g305: LineSegment StartX=50.5414 StartY=18.6536 StartZ=0 EndX=50.5381 EndY=18.7381 EndZ=0
    g306: LineSegment StartX=50.5381 StartY=18.7381 StartZ=0 EndX=50.4114 EndY=18.7218 EndZ=0
    g307: LineSegment StartX=50.4114 StartY=18.7218 StartZ=0 EndX=50.3951 EndY=18.7934 EndZ=0
    g308: LineSegment StartX=50.3951 StartY=18.7934 StartZ=0 EndX=50.3334 EndY=18.7934 EndZ=0
    g309: LineSegment StartX=50.3334 StartY=18.7934 StartZ=0 EndX=50.3366 EndY=18.8389 EndZ=0
    g310: LineSegment StartX=50.3366 StartY=18.8389 StartZ=0 EndX=50.2066 EndY=18.8389 EndZ=0
    g311: LineSegment StartX=50.2066 StartY=18.8389 StartZ=0 EndX=50.2099 EndY=18.9201 EndZ=0
    g312: LineSegment StartX=50.2099 StartY=18.9201 StartZ=0 EndX=50.1254 EndY=18.9266 EndZ=0
    g313: LineSegment StartX=50.1254 StartY=18.9266 StartZ=0 EndX=50.1156 EndY=19.0046 EndZ=0
    g314: LineSegment StartX=50.1156 StartY=19.0046 StartZ=0 EndX=49.9986 EndY=18.9949 EndZ=0
    g315: LineSegment StartX=49.9986 StartY=18.9949 StartZ=0 EndX=49.9921 EndY=19.0859 EndZ=0
    g316: LineSegment StartX=49.9921 StartY=19.0859 StartZ=0 EndX=49.9368 EndY=19.0501 EndZ=0
    g317: LineSegment StartX=49.9368 StartY=19.0501 StartZ=0 EndX=49.9206 EndY=19.1509 EndZ=0
    g318: LineSegment StartX=49.9206 StartY=19.1509 StartZ=0 EndX=49.7971 EndY=19.1281 EndZ=0
    g319: LineSegment StartX=49.7971 StartY=19.1281 StartZ=0 EndX=49.8068 EndY=19.2029 EndZ=0
    g320: LineSegment StartX=49.8068 StartY=19.2029 StartZ=0 EndX=49.7288 EndY=19.1899 EndZ=0
    g321: LineSegment StartX=49.7288 StartY=19.1899 StartZ=0 EndX=49.7191 EndY=19.2582 EndZ=0
    g322: LineSegment StartX=49.7191 StartY=19.2582 StartZ=0 EndX=49.6606 EndY=19.2647 EndZ=0
    g323: LineSegment StartX=49.6606 StartY=19.2647 StartZ=0 EndX=49.6541 EndY=19.3329 EndZ=0
    g324: LineSegment StartX=49.6541 StartY=19.3329 StartZ=0 EndX=49.6021 EndY=19.3329 EndZ=0
    g325: LineSegment StartX=49.6021 StartY=19.3329 StartZ=0 EndX=49.5988 EndY=19.4077 EndZ=0
    g326: LineSegment StartX=49.5988 StartY=19.4077 StartZ=0 EndX=49.4623 EndY=19.3947 EndZ=0
    g327: LineSegment StartX=49.4623 StartY=19.3947 StartZ=0 EndX=49.4623 EndY=19.4727 EndZ=0
    g328: LineSegment StartX=49.4623 StartY=19.4727 StartZ=0 EndX=49.2543 EndY=19.4532 EndZ=0
    g329: LineSegment StartX=49.2543 StartY=19.4532 StartZ=0 EndX=49.2543 EndY=19.5279 EndZ=0
    g330: LineSegment StartX=49.2543 StartY=19.5279 StartZ=0 EndX=49.199 EndY=19.5279 EndZ=0
    g331: LineSegment StartX=49.199 StartY=19.5279 StartZ=0 EndX=49.199 EndY=19.6189 EndZ=0
    g332: LineSegment StartX=49.199 StartY=19.6189 StartZ=0 EndX=49.0658 EndY=19.6059 EndZ=0
    g333: LineSegment StartX=49.0658 StartY=19.6059 StartZ=0 EndX=49.0495 EndY=19.6612 EndZ=0
    g334: LineSegment StartX=49.0495 StartY=19.6612 StartZ=0 EndX=48.991 EndY=19.6547 EndZ=0
    g335: LineSegment StartX=48.991 StartY=19.6547 StartZ=0 EndX=48.9845 EndY=19.7359 EndZ=0
    g336: LineSegment StartX=48.9845 StartY=19.7359 StartZ=0 EndX=48.8577 EndY=19.7262 EndZ=0
    g337: LineSegment StartX=48.8577 StartY=19.7262 StartZ=0 EndX=48.8577 EndY=19.8149 EndZ=0
    g338: LineSegment StartX=48.8577 StartY=19.8149 StartZ=0 EndX=48.7743 EndY=19.8069 EndZ=0
    g339: LineSegment StartX=48.7743 StartY=19.8069 StartZ=0 EndX=48.7743 EndY=19.8894 EndZ=0
    g340: LineSegment StartX=48.7743 StartY=19.8894 StartZ=0 EndX=48.5854 EndY=19.8894 EndZ=0
    g341: LineSegment StartX=48.5854 StartY=19.8894 StartZ=0 EndX=48.5854 EndY=19.9533 EndZ=0
    g342: LineSegment StartX=48.5854 StartY=19.9533 StartZ=0 EndX=48.4417 EndY=19.9533 EndZ=0
    g343: LineSegment StartX=48.4417 StartY=19.9533 StartZ=0 EndX=48.4417 EndY=20.0118 EndZ=0
    g344: LineSegment StartX=48.4417 StartY=20.0118 StartZ=0 EndX=48.3751 EndY=20.0118 EndZ=0
    g345: LineSegment StartX=48.3751 StartY=20.0118 StartZ=0 EndX=48.3751 EndY=20.089 EndZ=0
    g346: LineSegment StartX=48.3751 StartY=20.089 StartZ=0 EndX=48.3033 EndY=20.089 EndZ=0
    g347: LineSegment StartX=48.3033 StartY=20.089 StartZ=0 EndX=48.3033 EndY=20.1524 EndZ=0
    g348: LineSegment StartX=48.3033 StartY=20.1524 StartZ=0 EndX=48.0916 EndY=20.1524 EndZ=0
    g349: LineSegment StartX=48.0916 StartY=20.1524 StartZ=0 EndX=48.0916 EndY=20.2331 EndZ=0
    g350: LineSegment StartX=48.0916 StartY=20.2331 StartZ=0 EndX=47.8912 EndY=20.2331 EndZ=0
    g351: LineSegment StartX=47.8912 StartY=20.2331 StartZ=0 EndX=47.8912 EndY=20.2962 EndZ=0
    g352: LineSegment StartX=47.8912 StartY=20.2962 StartZ=0 EndX=47.6864 EndY=20.2962 EndZ=0
    g353: LineSegment StartX=47.6864 StartY=20.2962 StartZ=0 EndX=47.6864 EndY=20.3681 EndZ=0
    g354: LineSegment StartX=47.6864 StartY=20.3681 StartZ=0 EndX=47.2898 EndY=20.3681 EndZ=0
    g355: LineSegment StartX=47.2898 StartY=20.3681 StartZ=0 EndX=47.2898 EndY=20.4313 EndZ=0
    g356: LineSegment StartX=47.2898 StartY=20.4313 StartZ=0 EndX=47.0094 EndY=20.4313 EndZ=0
    g357: LineSegment StartX=47.0094 StartY=20.4313 StartZ=0 EndX=47.0094 EndY=20.5033 EndZ=0
    g358: LineSegment StartX=47.0094 StartY=20.5033 StartZ=0 EndX=46.7265 EndY=20.5033 EndZ=0
    g359: LineSegment StartX=46.7265 StartY=20.5033 StartZ=0 EndX=46.7265 EndY=20.5623 EndZ=0
    g360: LineSegment StartX=46.7265 StartY=20.5623 StartZ=0 EndX=46.3195 EndY=20.5623 EndZ=0
    g361: LineSegment StartX=46.3195 StartY=20.5623 StartZ=0 EndX=46.2304 EndY=20.478 EndZ=0
    g362: LineSegment StartX=46.2304 StartY=20.478 StartZ=0 EndX=45.8403 EndY=20.478 EndZ=0
    g363: LineSegment StartX=45.8403 StartY=20.478 StartZ=0 EndX=45.7581 EndY=20.3987 EndZ=0
    g364: LineSegment StartX=45.7581 StartY=20.3987 StartZ=0 EndX=45.6847 EndY=20.3987 EndZ=0
    g365: LineSegment StartX=45.6847 StartY=20.3987 StartZ=0 EndX=45.6847 EndY=20.4757 EndZ=0
    g366: LineSegment StartX=45.6847 StartY=20.4757 StartZ=0 EndX=45.2353 EndY=20.4757 EndZ=0
    g367: LineSegment StartX=45.2353 StartY=20.4757 StartZ=0 EndX=45.1511 EndY=20.3964 EndZ=0
    g368: LineSegment StartX=45.1511 StartY=20.3964 StartZ=0 EndX=45.039 EndY=20.3905 EndZ=0
    g369: LineSegment StartX=45.1271 StartY=20.498 StartZ=0 EndX=45.039 EndY=20.3905 EndZ=0
    g370: LineSegment StartX=45.1271 StartY=20.498 StartZ=0 EndX=45.1672 EndY=20.498 EndZ=0
    g371: LineSegment StartX=45.1672 StartY=20.498 StartZ=0 EndX=45.2586 EndY=20.5605 EndZ=0
    g372: LineSegment StartX=45.2586 StartY=20.5605 StartZ=0 EndX=45.3242 EndY=20.5605 EndZ=0
    g373: LineSegment StartX=45.3242 StartY=20.5605 StartZ=0 EndX=45.4009 EndY=20.6461 EndZ=0
    g374: LineSegment StartX=45.4009 StartY=20.6461 StartZ=0 EndX=45.5221 EndY=20.6461 EndZ=0
    g375: LineSegment StartX=45.5221 StartY=20.6461 StartZ=0 EndX=45.6149 EndY=20.705 EndZ=0
    g376: LineSegment StartX=45.6149 StartY=20.705 StartZ=0 EndX=45.8042 EndY=20.705 EndZ=0
    g377: LineSegment StartX=45.8042 StartY=20.705 StartZ=0 EndX=45.9915 EndY=20.8898 EndZ=0
    g378: LineSegment StartX=45.9915 StartY=20.8898 StartZ=0 EndX=45.9915 EndY=20.959 EndZ=0
    g379: LineSegment StartX=45.9915 StartY=20.959 StartZ=0 EndX=46.0581 EndY=21.0202 EndZ=0
    g380: LineSegment StartX=46.0581 StartY=21.0202 StartZ=0 EndX=46.0527 EndY=21.0894 EndZ=0
    g381: LineSegment StartX=46.0527 StartY=21.0894 StartZ=0 EndX=46.2124 EndY=21.2464 EndZ=0
    g382: LineSegment StartX=46.2124 StartY=21.2464 StartZ=0 EndX=46.2763 EndY=21.2277 EndZ=0
    g383: LineSegment StartX=46.2763 StartY=21.2277 StartZ=0 EndX=46.5051 EndY=21.4486 EndZ=0
    g384: LineSegment StartX=46.5051 StartY=21.4486 StartZ=0 EndX=46.585 EndY=21.4539 EndZ=0
    g385: LineSegment StartX=46.585 StartY=21.4539 StartZ=0 EndX=46.6994 EndY=21.603 EndZ=0
    g386: LineSegment StartX=46.6994 StartY=21.603 StartZ=0 EndX=46.8245 EndY=21.5843 EndZ=0
    g387: LineSegment StartX=46.8245 StartY=21.5843 StartZ=0 EndX=46.9016 EndY=21.6855 EndZ=0
    g388: LineSegment StartX=46.9016 StartY=21.6855 StartZ=0 EndX=46.9655 EndY=21.6562 EndZ=0
    g389: LineSegment StartX=46.9655 StartY=21.6562 StartZ=0 EndX=47.205 EndY=21.8754 EndZ=0
    g390: LineSegment StartX=47.205 StartY=21.8754 StartZ=0 EndX=47.205 EndY=22.0711 EndZ=0
    g391: LineSegment StartX=47.205 StartY=22.0711 StartZ=0 EndX=47.2634 EndY=22.0711 EndZ=0
    g392: LineSegment StartX=47.2634 StartY=22.0711 StartZ=0 EndX=47.6208 EndY=22.4458 EndZ=0
    g393: LineSegment StartX=47.6208 StartY=22.4458 StartZ=0 EndX=47.6208 EndY=22.5177 EndZ=0
    g394: LineSegment StartX=47.6208 StartY=22.5177 StartZ=0 EndX=47.8212 EndY=22.7182 EndZ=0
    g395: LineSegment StartX=47.8212 StartY=22.7182 StartZ=0 EndX=47.8343 EndY=22.7944 EndZ=0
    g396: LineSegment StartX=47.8343 StartY=22.7944 StartZ=0 EndX=48.0478 EndY=22.997 EndZ=0
    g397: LineSegment StartX=48.0478 StartY=22.997 StartZ=0 EndX=48.0478 EndY=23.1365 EndZ=0
    g398: LineSegment StartX=48.0478 StartY=23.1365 StartZ=0 EndX=48.0998 EndY=23.2173 EndZ=0
    g399: LineSegment StartX=48.0998 StartY=23.2173 StartZ=0 EndX=48.0998 EndY=23.2802 EndZ=0
    ... +484 more geometry lines
  constraints (1492):
    c: Coincident(g3,g2)
    c: Vertical(g4)
    c: Vertical(g6)
    c: Coincident(g8,g7)
    c: Vertical(g8)
    c: Coincident(g8,g9)
    c: Coincident(g9,g10)
    c: Vertical(g10)
    c: Coincident(g10,g11)
    c: Coincident(g11,g12)
    c: Vertical(g12)
    c: Coincident(g13,g12)
    c: Horizontal(g13)
    c: Vertical(g14)
    c: Coincident(g16,g15)
    c: Vertical(g16)
    c: Horizontal(g17)
    c: Coincident(g18,g17)
    c: Vertical(g18)
    c: Horizontal(g19)
    c: Coincident(g20,g19)
    c: Vertical(g20)
    c: Horizontal(g21)
    c: Vertical(g22)
    c: Horizontal(g23)
    c: Coincident(g24,g23)
    c: Vertical(g24)
    c: Horizontal(g25)
    c: Coincident(g27,g26)
    c: Horizontal(g27)
    c: Vertical(g28)
    c: Coincident(g30,g29)
    c: Vertical(g30)
    c: Coincident(g31,g32)
    c: Vertical(g32)
    c: Coincident(g32,g33)
    c: Horizontal(g33)
    c: Coincident(g34,g33)
    c: Vertical(g34)
    c: Coincident(g35,g34)
    c: Horizontal(g35)
    c: Coincident(g36,g35)
    c: Vertical(g36)
    c: Coincident(g37,g36)
    c: Horizontal(g37)
    c: Vertical(g38)
    c: Horizontal(g39)
    c: Vertical(g40)
    c: Horizontal(g41)
    c: Coincident(g42,g41)
    c: Vertical(g42)
    c: Horizontal(g43)
    c: Coincident(g44,g43)
    c: Vertical(g44)
    c: Coincident(g45,g44)
    c: Horizontal(g45)
    c: Coincident(g46,g45)
    c: Vertical(g46)
    c: Coincident(g47,g46)
    c: Horizontal(g47)
    c: Coincident(g48,g47)
    c: Vertical(g48)
    c: Horizontal(g49)
    c: Vertical(g50)
    c: Coincident(g51,g50)
    c: Horizontal(g51)
    c: Vertical(g52)
    c: Coincident(g53,g52)
    c: Horizontal(g53)
    c: Coincident(g54,g53)
    c: Vertical(g54)
    c: Coincident(g55,g54)
    c: Horizontal(g55)
    c: Coincident(g56,g55)
    c: Vertical(g56)
    c: Coincident(g57,g56)
    c: Horizontal(g57)
    c: Coincident(g58,g57)
    c: Vertical(g58)
    c: Coincident(g60,g59)
    c: Vertical(g60)
    c: Coincident(g61,g60)
    c: Horizontal(g61)
    c: Vertical(g62)
    c: Horizontal(g63)
    c: Coincident(g64,g63)
    c: Vertical(g64)
    c: Horizontal(g65)
    c: Vertical(g66)
    c: Coincident(g68,g67)
    c: Vertical(g68)
    c: Horizontal(g69)
    c: Coincident(g70,g69)
    c: Vertical(g70)
    c: Horizontal(g71)
    c: Coincident(g72,g71)
    c: Vertical(g72)
    c: Horizontal(g73)
    c: Coincident(g74,g73)
    c: Vertical(g74)
    c: Horizontal(g75)
    c: Coincident(g76,g75)
    c: Vertical(g76)
    c: Horizontal(g77)
    c: Vertical(g78)
    c: Coincident(g79,g78)
    c: Coincident(g80,g79)
    c: Vertical(g80)
    c: Coincident(g81,g80)
    c: Coincident(g82,g81)
    c: Horizontal(g83)
    c: Coincident(g85,g84)
    c: Horizontal(g85)
    c: Coincident(g86,g85)
    c: Coincident(g89,g88)
    c: Horizontal(g89)
    c: Coincident(g90,g89)
    c: Coincident(g91,g90)
    c: Horizontal(g91)
    c: Coincident(g92,g91)
    c: Horizontal(g93)
    c: Coincident(g94,g93)
    c: Horizontal(g95)
    c: Coincident(g96,g95)
    c: Coincident(g97,g98)
    c: Coincident(g98,g99)
    c: Vertical(g99)
    c: Coincident(g99,g100)
    c: Coincident(g100,g101)
    c: Coincident(g101,g102)
    c: Coincident(g102,g103)
    c: Coincident(g103,g104)
    c: Coincident(g104,g105)
    c: Vertical(g105)
    c: Coincident(g105,g106)
    c: Coincident(g106,g107)
    c: Coincident(g107,g108)
    c: Horizontal(g108)
    c: Coincident(g108,g109)
    c: Coincident(g109,g110)
    c: Vertical(g110)
    c: Coincident(g110,g111)
    c: Coincident(g111,g112)
    c: Coincident(g112,g113)
    c: Coincident(g113,g114)
    c: Coincident(g114,g115)
    c: Coincident(g115,g116)
    c: Vertical(g116)
    c: Coincident(g116,g117)
    c: Coincident(g117,g118)
    c: Coincident(g118,g119)
    c: Coincident(g119,g120)
    c: Coincident(g120,g121)
    c: Horizontal(g121)
    c: Coincident(g121,g122)
    c: Coincident(g122,g123)
    c: Coincident(g123,g124)
    c: Coincident(g124,g125)
    c: Vertical(g125)
    c: Coincident(g125,g126)
    c: Coincident(g126,g127)
    c: Horizontal(g127)
    c: Coincident(g127,g128)
    c: Vertical(g128)
    c: Coincident(g128,g129)
    c: Coincident(g129,g130)
    c: Vertical(g130)
    c: Coincident(g130,g131)
    c: Horizontal(g131)
    c: Coincident(g131,g132)
    c: Vertical(g132)
    c: Coincident(g132,g133)
    c: Coincident(g133,g134)
    c: Coincident(g134,g135)
    c: Coincident(g135,g136)
    c: Coincident(g136,g137)
    c: Coincident(g137,g138)
    c: Vertical(g138)
    c: Coincident(g138,g139)
    c: Coincident(g139,g140)
    c: Vertical(g140)
    c: Coincident(g140,g141)
    c: Horizontal(g141)
    c: Coincident(g141,g142)
    c: Coincident(g142,g143)
    c: Coincident(g143,g144)
    c: Coincident(g144,g145)
    c: Coincident(g145,g146)
    c: Vertical(g146)
    c: Coincident(g146,g147)
    c: Coincident(g147,g148)
    c: Vertical(g148)
    c: Coincident(g148,g149)
    c: Horizontal(g149)
    c: Coincident(g149,g150)
    c: Vertical(g150)
    c: Coincident(g150,g151)
    c: Horizontal(g151)
    c: Coincident(g151,g152)
    c: Vertical(g152)
    c: Coincident(g152,g153)
    c: Horizontal(g153)
    c: Coincident(g153,g154)
    c: Vertical(g154)
    c: Coincident(g154,g155)
    c: Horizontal(g155)
    c: Coincident(g155,g156)
    c: Vertical(g156)
    c: Coincident(g156,g157)
    c: Horizontal(g157)
    c: Coincident(g157,g158)
    c: Vertical(g158)
    c: Coincident(g158,g159)
    c: Coincident(g159,g160)
    c: Coincident(g160,g161)
    c: Horizontal(g161)
    c: Coincident(g161,g162)
    c: Vertical(g162)
    c: Coincident(g162,g163)
    c: Horizontal(g163)
    c: Coincident(g163,g164)
    c: Coincident(g164,g165)
    c: Horizontal(g165)
    c: Coincident(g165,g166)
    c: Vertical(g166)
    c: Coincident(g166,g167)
    c: Horizontal(g167)
    c: Coincident(g167,g168)
    c: Coincident(g168,g169)
    c: Coincident(g169,g170)
    c: Vertical(g170)
    c: Coincident(g170,g171)
    c: Coincident(g171,g172)
    c: Vertical(g172)
    c: Coincident(g172,g173)
    c: Horizontal(g173)
    c: Coincident(g173,g174)
    c: Vertical(g174)
    c: Coincident(g174,g175)
    c: Horizontal(g175)
    c: Coincident(g175,g176)
    c: Vertical(g176)
    c: Coincident(g176,g177)
    c: Coincident(g177,g178)
    c: Vertical(g178)
    c: Coincident(g178,g179)
    c: Horizontal(g179)
    c: Coincident(g179,g180)
    c: Vertical(g180)
    c: Coincident(g180,g181)
    c: Horizontal(g181)
    c: Coincident(g181,g182)
    c: Vertical(g182)
    c: Coincident(g182,g183)
    c: Horizontal(g183)
    c: Coincident(g183,g184)
    c: Vertical(g184)
    c: Coincident(g184,g185)
    c: Horizontal(g185)
    c: Coincident(g185,g186)
    c: Coincident(g186,g187)
    c: Coincident(g187,g188)
    c: Coincident(g188,g189)
    c: Vertical(g189)
    c: Coincident(g189,g190)
    c: Coincident(g190,g191)
    c: Coincident(g191,g192)
    c: Coincident(g192,g193)
    c: Coincident(g193,g194)
    c: Coincident(g194,g195)
    c: Vertical(g195)
    c: Coincident(g195,g196)
    c: Coincident(g196,g197)
    c: Vertical(g197)
    c: Coincident(g197,g198)
    c: Coincident(g198,g199)
    c: Vertical(g199)
    c: Coincident(g199,g200)
    c: Coincident(g200,g201)
    c: Vertical(g201)
    c: Coincident(g201,g202)
    c: Coincident(g202,g203)
    c: Vertical(g203)
    c: Coincident(g203,g204)
    c: Coincident(g204,g205)
    c: Vertical(g205)
    c: Coincident(g205,g206)
    c: Coincident(g206,g207)
    c: Coincident(g207,g208)
    c: Coincident(g208,g209)
    c: Vertical(g209)
    c: Coincident(g209,g210)
    c: Coincident(g210,g211)
    c: Coincident(g211,g212)
    c: Coincident(g212,g213)
    c: Coincident(g213,g214)
    c: Coincident(g214,g215)
    c: Vertical(g215)
    c: Coincident(g215,g216)
    c: Coincident(g216,g217)
    c: Horizontal(g217)
    c: Coincident(g217,g218)
    c: Vertical(g218)
    c: Coincident(g218,g219)
    c: Horizontal(g219)
    c: Coincident(g219,g220)
    c: Coincident(g220,g221)
    c: Horizontal(g221)
    c: Coincident(g221,g222)
    c: Coincident(g222,g223)
    c: Horizontal(g223)
    c: Coincident(g223,g224)
    c: Coincident(g224,g225)
    c: Horizontal(g225)
    c: Coincident(g225,g226)
    c: Vertical(g226)
    c: Coincident(g226,g227)
    c: Horizontal(g227)
    c: Coincident(g227,g228)
    c: Vertical(g228)
    c: Coincident(g228,g229)
    c: Horizontal(g229)
    c: Coincident(g229,g230)
    c: Coincident(g230,g231)
    c: Coincident(g231,g232)
    c: Coincident(g232,g233)
    c: Horizontal(g233)
    c: Coincident(g233,g234)
    c: Coincident(g234,g235)
    c: Horizontal(g235)
    c: Coincident(g235,g236)
    c: Coincident(g236,g237)
    c: Horizontal(g237)
    c: Coincident(g237,g238)
    c: Coincident(g238,g239)
    c: Horizontal(g239)
    c: Coincident(g239,g240)
    c: Coincident(g240,g241)
    c: Vertical(g241)
    c: Coincident(g241,g242)
    c: Horizontal(g242)
    c: Coincident(g242,g243)
    c: Vertical(g243)
    c: Coincident(g243,g244)
    c: Coincident(g244,g245)
    c: Vertical(g245)
    c: Coincident(g245,g246)
    c: Horizontal(g246)
    c: Coincident(g246,g247)
    c: Coincident(g247,g248)
    c: Horizontal(g248)
    c: Coincident(g248,g249)
    c: Vertical(g249)
    c: Coincident(g249,g250)
    c: Coincident(g250,g251)
    c: Coincident(g251,g252)
    c: Horizontal(g252)
    c: Coincident(g252,g253)
    c: Coincident(g253,g254)
    c: Horizontal(g254)
    c: Coincident(g254,g255)
    c: Vertical(g255)
    c: Coincident(g255,g256)
    c: Coincident(g256,g257)
    c: Coincident(g257,g258)
    c: Coincident(g258,g259)
    c: Coincident(g259,g260)
    c: Coincident(g260,g261)
    c: Vertical(g257)
    c: Horizontal(g258)
    c: Horizontal(g256)
    c: Vertical(g259)
    c: Horizontal(g260)
    c: Vertical(g261)
    c: Coincident(g261,g262)
    c: Horizontal(g262)
    c: Coincident(g262,g263)
    c: Vertical(g263)
    c: Coincident(g263,g264)
    c: Coincident(g264,g265)
    c: Coincident(g265,g266)
    c: Coincident(g266,g267)
    c: Coincident(g267,g268)
    c: Coincident(g268,g269)
    c: Vertical(g269)
    c: Coincident(g269,g270)
    c: Horizontal(g270)
    c: Coincident(g270,g271)
    c: Vertical(g271)
    c: Coincident(g271,g272)
    c: Coincident(g272,g273)
    c: Vertical(g273)
    c: Coincident(g273,g274)
    c: Horizontal(g274)
    c: Coincident(g274,g275)
    c: Vertical(g275)
    c: Coincident(g275,g276)
    c: Horizontal(g276)
    c: Coincident(g276,g277)
    c: Coincident(g277,g278)
    c: Horizontal(g278)
    c: Coincident(g278,g279)
    c: Coincident(g279,g280)
    c: Coincident(g280,g281)
    c: Vertical(g281)
    c: Coincident(g281,g282)
    c: Coincident(g282,g283)
    c: Coincident(g283,g284)
    c: Horizontal(g284)
    c: Coincident(g284,g285)
    c: Coincident(g285,g286)
    c: Coincident(g286,g287)
    c: Coincident(g287,g288)
    c: Coincident(g288,g289)
    c: Coincident(g289,g290)
    c: Coincident(g290,g291)
    c: Vertical(g291)
    c: Coincident(g291,g292)
    c: Horizontal(g292)
    c: Coincident(g292,g293)
    c: Coincident(g293,g294)
    c: Horizontal(g294)
    c: Coincident(g294,g295)
    c: Vertical(g295)
    c: Coincident(g295,g296)
    c: Coincident(g296,g297)
    c: Vertical(g297)
    c: Coincident(g297,g298)
    c: Horizontal(g298)
    c: Coincident(g298,g299)
    c: Vertical(g299)
    c: Coincident(g299,g300)
    c: Horizontal(g300)
    c: Coincident(g300,g301)
    c: Coincident(g301,g302)
    c: Coincident(g302,g303)
    c: Coincident(g303,g304)
    c: Coincident(g304,g305)
    c: Coincident(g305,g306)
    c: Coincident(g306,g307)
    c: Coincident(g307,g308)
    c: Horizontal(g308)
    c: Coincident(g308,g309)
    c: Coincident(g309,g310)
    c: Horizontal(g310)
    c: Coincident(g310,g311)
    c: Coincident(g311,g312)
    c: Coincident(g312,g313)
    c: Coincident(g313,g314)
    c: Coincident(g314,g315)
    c: Coincident(g315,g316)
    c: Coincident(g316,g317)
    c: Coincident(g317,g318)
    c: Coincident(g318,g319)
    c: Coincident(g319,g320)
    c: Coincident(g320,g321)
    c: Coincident(g321,g322)
    c: Coincident(g322,g323)
    c: Coincident(g323,g324)
    c: Horizontal(g324)
    c: Coincident(g324,g325)
    c: Coincident(g325,g326)
    c: Coincident(g326,g327)
    c: Vertical(g327)
    c: Coincident(g327,g328)
    c: Coincident(g328,g329)
    c: Coincident(g329,g330)
    c: Coincident(g330,g331)
    c: Vertical(g331)
    c: Coincident(g331,g332)
    c: Coincident(g332,g333)
    c: Coincident(g333,g334)
    c: Coincident(g334,g335)
    c: Coincident(g335,g336)
    c: Coincident(g336,g337)
    c: Vertical(g337)
    c: Coincident(g337,g338)
    c: Coincident(g338,g339)
    c: Coincident(g339,g340)
    c: Coincident(g340,g341)
    c: Coincident(g341,g342)
    c: Coincident(g342,g343)
    c: Coincident(g343,g344)
    c: Coincident(g344,g345)
    c: Coincident(g345,g346)
    c: Coincident(g346,g347)
    c: Coincident(g347,g348)
    c: Coincident(g348,g349)
    c: Coincident(g349,g350)
    c: Coincident(g350,g351)
    c: Coincident(g351,g352)
    c: Coincident(g352,g353)
    c: Coincident(g353,g354)
    c: Coincident(g354,g355)
    c: Coincident(g355,g356)
    c: Coincident(g356,g357)
    c: Vertical(g357)
    c: Coincident(g357,g358)
    c: Horizontal(g358)
    c: Coincident(g358,g359)
    c: Coincident(g359,g360)
    c: Coincident(g360,g361)
    c: Coincident(g361,g362)
    c: Horizontal(g362)
    c: Coincident(g362,g363)
    c: Coincident(g363,g364)
    c: Coincident(g364,g365)
    c: Coincident(g365,g366)
    c: Coincident(g366,g367)
    c: Horizontal(g290)
    c: Vertical(g287)
    c: Vertical(g285)
    c: Vertical(g283)
    c: Vertical(g279)
    c: Vertical(g277)
    c: Horizontal(g286)
    c: Horizontal(g288)
    c: Vertical(g289)
    c: Horizontal(g280)
    c: Horizontal(g282)
    c: Vertical(g329)
    c: Horizontal(g330)
    c: Horizontal(g340)
    c: Horizontal(g342)
    c: Horizontal(g344)
    c: Horizontal(g346)
    c: Horizontal(g348)
    c: Horizontal(g350)
    c: Vertical(g339)
    c: Vertical(g341)
    c: Vertical(g343)
    c: Vertical(g345)
    c: Vertical(g347)
    c: Vertical(g349)
    c: Vertical(g351)
    c: Vertical(g353)
    c: Vertical(g355)
    c: Horizontal(g352)
    c: Horizontal(g354)
    c: Horizontal(g356)
    c: Vertical(g359)
    c: Horizontal(g360)
    c: Horizontal(g364)
    c: Vertical(g365)
    c: Horizontal(g366)
    c: Coincident(g368,g367)
    c: Coincident(g369,g368)
    c: Coincident(g369,g370)
    c: Coincident(g370,g371)
    c: Coincident(g371,g372)
    c: Horizontal(g372)
    c: Coincident(g372,g373)
    c: Coincident(g373,g374)
    c: Coincident(g374,g375)
    c: Coincident(g375,g376)
    c: Coincident(g376,g377)
    c: Coincident(g377,g378)
    c: Vertical(g378)
    c: Coincident(g378,g379)
    c: Coincident(g379,g380)
    c: Coincident(g380,g381)
    c: Coincident(g381,g382)
    c: Coincident(g382,g383)
    c: Coincident(g383,g384)
    c: Coincident(g384,g385)
    c: Coincident(g385,g386)
    c: Coincident(g386,g387)
    c: Coincident(g387,g388)
    c: Coincident(g388,g389)
    c: Coincident(g389,g390)
    c: Coincident(g390,g391)
    c: Horizontal(g391)
    c: Coincident(g391,g392)
    c: Coincident(g392,g393)
    c: Coincident(g393,g394)
    c: Coincident(g394,g395)
    c: Coincident(g395,g396)
    c: Coincident(g396,g397)
    c: Coincident(g397,g398)
    c: Coincident(g398,g399)
    c: Coincident(g399,g400)
    c: Coincident(g400,g401)
    c: Coincident(g401,g402)
    c: Coincident(g402,g403)
    c: Coincident(g403,g404)
    c: Coincident(g404,g405)
    c: Coincident(g405,g406)
    c: Coincident(g406,g407)
    c: Coincident(g407,g408)
    c: Coincident(g408,g409)
    c: Vertical(g409)
    c: Coincident(g409,g410)
    c: Coincident(g410,g411)
    c: Vertical(g411)
    c: Coincident(g411,g412)
    c: Horizontal(g412)
    c: Coincident(g412,g413)
    c: Coincident(g413,g414)
    c: Horizontal(g414)
    c: Coincident(g414,g415)
    c: Coincident(g415,g416)
    c: Coincident(g416,g417)
    c: Coincident(g417,g418)
    c: Coincident(g418,g419)
    c: Coincident(g419,g420)
    c: Coincident(g420,g421)
    c: Coincident(g421,g422)
    c: Coincident(g422,g423)
    c: Coincident(g423,g424)
    c: Coincident(g424,g425)
    c: Coincident(g425,g426)
    c: Horizontal(g426)
    c: Coincident(g426,g427)
    c: Coincident(g427,g428)
    c: Horizontal(g428)
    c: Coincident(g428,g429)
    c: Coincident(g429,g430)
    c: Coincident(g430,g431)
    c: Coincident(g431,g432)
    c: Horizontal(g432)
    c: Coincident(g432,g433)
    c: Coincident(g433,g434)
    c: Horizontal(g434)
    c: Coincident(g434,g435)
    c: Coincident(g435,g436)
    c: Coincident(g436,g437)
    c: Coincident(g437,g438)
    c: Coincident(g439,g440)
    c: Coincident(g440,g441)
    c: Coincident(g441,g442)
    c: Coincident(g442,g443)
    c: Coincident(g443,g444)
    c: Coincident(g444,g445)
    c: Coincident(g445,g446)
    c: Coincident(g446,g447)
    c: Coincident(g447,g448)
    c: Coincident(g448,g449)
    c: Coincident(g449,g450)
    c: Coincident(g450,g451)
    c: Coincident(g451,g452)
    c: Coincident(g452,g453)
    c: Coincident(g453,g454)
    c: Coincident(g454,g455)
    c: Coincident(g455,g456)
    c: Coincident(g456,g457)
    c: Coincident(g457,g458)
    c: Coincident(g458,g459)
    c: Coincident(g459,g460)
    c: Coincident(g460,g461)
    c: Coincident(g461,g462)
    c: Coincident(g462,g463)
    c: Coincident(g463,g464)
    c: Coincident(g464,g465)
    c: Coincident(g465,g466)
    c: Coincident(g466,g467)
    c: Coincident(g467,g468)
    c: Coincident(g468,g469)
    c: Coincident(g469,g470)
    c: Coincident(g470,g471)
    c: Coincident(g471,g472)
    c: Horizontal(g472)
    c: Coincident(g472,g473)
    c: Coincident(g473,g474)
    c: Coincident(g474,g475)
    c: Coincident(g475,g476)
    c: Coincident(g476,g477)
    c: Coincident(g477,g478)
    c: Coincident(g478,g479)
    c: Coincident(g479,g480)
    c: Coincident(g480,g481)
    c: Coincident(g481,g482)
    c: Coincident(g482,g483)
    c: Coincident(g483,g484)
    c: Coincident(g484,g485)
    c: Coincident(g485,g486)
    c: Coincident(g486,g487)
    c: Coincident(g487,g488)
    c: Vertical(g488)
    c: Coincident(g488,g489)
    c: Coincident(g489,g490)
    c: Vertical(g490)
    c: Coincident(g490,g491)
    c: Coincident(g491,g492)
    c: Coincident(g492,g493)
    c: Coincident(g493,g494)
    c: Coincident(g494,g495)
    c: Coincident(g495,g496)
    c: Coincident(g496,g497)
    c: Coincident(g497,g498)
    c: Coincident(g498,g499)
    c: Coincident(g499,g500)
    c: Coincident(g500,g501)
    c: Coincident(g501,g502)
    c: Coincident(g502,g503)
    c: Coincident(g503,g504)
    c: Horizontal(g370)
    c: Horizontal(g374)
    c: Horizontal(g376)
    c: Vertical(g390)
    c: Vertical(g397)
    c: Vertical(g399)
    c: Vertical(g401)
    c: Vertical(g403)
    c: Vertical(g407)
    c: Horizontal(g410)
    c: Vertical(g413)
    c: Vertical(g415)
    c: Horizontal(g416)
    c: Vertical(g417)
    c: Horizontal(g418)
    c: Vertical(g419)
    c: Vertical(g421)
    c: Vertical(g423)
    c: Vertical(g425)
    c: Vertical(g427)
    c: Vertical(g429)
    c: Horizontal(g420)
    c: Horizontal(g422)
    c: Horizontal(g424)
    c: Vertical(g431)
    c: Vertical(g433)
    c: Vertical(g435)
    c: Horizontal(g436)
    c: Horizontal(g438)
    c: Vertical(g437)
    c: Coincident(g439,g505)
    c: Horizontal(g505)
    c: Coincident(g505,g506)
    c: Coincident(g506,g438)
    c: Vertical(g506)
    c: Horizontal(g464)
    c: Horizontal(g462)
    c: Horizontal(g460)
    c: Horizontal(g458)
    c: Horizontal(g456)
    c: Horizontal(g454)
    c: Horizontal(g452)
    c: Horizontal(g450)
    c: Horizontal(g448)
    c: Horizontal(g446)
    c: Horizontal(g444)
    c: Horizontal(g442)
    c: Horizontal(g440)
    c: Horizontal(g468)
    c: Horizontal(g470)
    c: Horizontal(g474)
    c: Horizontal(g476)
    c: Horizontal(g478)
    c: Vertical(g465)
    c: Horizontal(g466)
    c: Vertical(g475)
    c: Vertical(g477)
    c: Horizontal(g491)
    c: Horizontal(g496)
    c: Horizontal(g494)
    c: Horizontal(g498)
    c: Vertical(g499)
    c: Vertical(g497)
    c: Vertical(g495)
    c: Vertical(g493)
    c: Horizontal(g500)
    c: Horizontal(g502)
    c: Horizontal(g504)
    c: Vertical(g501)
    c: Vertical(g503)
    c: Coincident(g504,g507)
    c: Vertical(g507)
    c: Coincident(g507,g508)
    c: Coincident(g508,g509)
    c: Coincident(g509,g510)
    c: Coincident(g510,g511)
    c: Vertical(g511)
    c: Coincident(g511,g512)
    c: Horizontal(g512)
    c: Coincident(g512,g513)
    c: Vertical(g513)
    c: Coincident(g513,g514)
    c: Coincident(g514,g515)
    c: Vertical(g515)
    c: Coincident(g515,g516)
    c: Horizontal(g516)
    c: Coincident(g516,g517)
    c: Coincident(g517,g518)
    c: Horizontal(g518)
    c: Coincident(g518,g519)
    c: Coincident(g519,g520)
    c: Coincident(g521,g522)
    c: Coincident(g522,g523)
    c: Coincident(g523,g524)
    c: Coincident(g524,g525)
    c: Coincident(g525,g526)
    c: Coincident(g526,g527)
    c: Coincident(g527,g528)
    c: Coincident(g528,g529)
    c: Coincident(g529,g530)
    c: Coincident(g531,g532)
    c: Coincident(g532,g533)
    c: Coincident(g533,g534)
    c: Coincident(g534,g535)
    c: Coincident(g535,g536)
    c: Coincident(g536,g537)
    c: Coincident(g537,g538)
    c: Coincident(g538,g539)
    c: Coincident(g539,g540)
    c: Coincident(g540,g541)
    c: Coincident(g541,g542)
    c: Coincident(g542,g543)
    c: Coincident(g543,g544)
    c: Coincident(g544,g545)
    c: Coincident(g545,g546)
    c: Coincident(g546,g547)
    c: Coincident(g547,g548)
    c: Coincident(g548,g549)
    c: Coincident(g549,g550)
    c: Horizontal(g550)
    c: Coincident(g550,g551)
    c: Coincident(g551,g552)
    c: Coincident(g552,g553)
    c: Coincident(g553,g554)
    c: Horizontal(g554)
    c: Coincident(g554,g555)
    c: Coincident(g555,g556)
    c: Coincident(g556,g557)
    c: Coincident(g557,g558)
    c: Horizontal(g558)
    c: Coincident(g558,g559)
    c: Coincident(g559,g560)
    c: Coincident(g560,g561)
    c: Coincident(g562,g563)
    c: Horizontal(g563)
    c: Coincident(g563,g564)
    c: Coincident(g564,g565)
    c: Coincident(g565,g566)
    c: Coincident(g566,g567)
    c: Horizontal(g567)
    c: Coincident(g567,g568)
    c: Coincident(g568,g569)
    c: Coincident(g569,g570)
    c: Coincident(g570,g571)
    c: Coincident(g571,g572)
    c: Coincident(g572,g573)
    c: Coincident(g573,g574)
    c: Coincident(g574,g575)
    c: Coincident(g575,g576)
    c: Coincident(g576,g577)
    c: Coincident(g577,g578)
    c: Coincident(g578,g579)
    c: Coincident(g579,g580)
    c: Vertical(g580)
    c: Coincident(g580,g581)
    c: Coincident(g581,g582)
    c: Coincident(g582,g583)
    c: Coincident(g583,g584)
    c: Coincident(g584,g585)
    c: Horizontal(g585)
    c: Coincident(g585,g586)
    c: Coincident(g586,g587)
    c: Coincident(g587,g588)
    c: Vertical(g588)
    c: Coincident(g588,g589)
    c: Coincident(g589,g590)
    c: Coincident(g590,g591)
    c: Coincident(g592,g593)
    c: Horizontal(g593)
    c: Coincident(g593,g594)
    c: Coincident(g594,g595)
    c: Coincident(g595,g596)
    c: Vertical(g596)
    c: Coincident(g596,g597)
    c: Horizontal(g597)
    c: Coincident(g597,g598)
    c: Vertical(g598)
    c: Coincident(g598,g599)
    c: Coincident(g599,g600)
    c: Coincident(g600,g601)
    c: Horizontal(g601)
    c: Coincident(g601,g602)
    c: Coincident(g602,g603)
    c: Coincident(g603,g604)
    c: Coincident(g604,g605)
    c: Coincident(g605,g606)
    c: Coincident(g606,g607)
    c: Coincident(g607,g608)
    c: Coincident(g608,g609)
    c: Horizontal(g609)
    c: Coincident(g609,g610)
    c: Coincident(g610,g611)
    c: Coincident(g611,g612)
    c: Coincident(g612,g613)
    c: Vertical(g613)
    c: Coincident(g613,g614)
    c: Coincident(g614,g615)
    c: Vertical(g615)
    c: Coincident(g615,g616)
    c: Coincident(g616,g617)
    c: Vertical(g617)
    c: Coincident(g618,g619)
    c: Vertical(g619)
    c: Coincident(g619,g620)
    c: Coincident(g620,g621)
    c: Coincident(g621,g622)
    c: Coincident(g622,g623)
    c: Coincident(g623,g624)
    c: Coincident(g624,g625)
    c: Coincident(g625,g626)
    c: Coincident(g626,g627)
    c: Vertical(g627)
    c: Coincident(g627,g628)
    c: Coincident(g628,g629)
    c: Coincident(g629,g630)
    c: Coincident(g630,g631)
    c: Coincident(g631,g632)
    c: Coincident(g632,g633)
    c: Vertical(g633)
    c: Coincident(g633,g634)
    c: Coincident(g634,g635)
    c: Vertical(g635)
    c: Coincident(g635,g636)
    c: Coincident(g636,g637)
    c: Coincident(g637,g638)
    c: Coincident(g638,g639)
    c: Coincident(g639,g640)
    c: Horizontal(g640)
    c: Coincident(g640,g641)
    c: Coincident(g641,g642)
    c: Vertical(g642)
    c: Coincident(g642,g643)
    c: Coincident(g643,g644)
    c: Vertical(g644)
    c: Coincident(g644,g645)
    c: Coincident(g645,g646)
    c: Coincident(g646,g647)
    c: Coincident(g647,g648)
    c: Coincident(g648,g649)
    c: Coincident(g649,g650)
    c: Coincident(g650,g651)
    c: Coincident(g651,g652)
    c: Vertical(g652)
    c: Coincident(g652,g653)
    c: Coincident(g653,g654)
    c: Coincident(g654,g655)
    c: Coincident(g655,g656)
    c: Coincident(g656,g657)
    c: Coincident(g657,g658)
    c: Vertical(g658)
    c: Coincident(g658,g659)
    c: Coincident(g659,g660)
    c: Vertical(g660)
    c: Coincident(g660,g661)
    c: Coincident(g661,g662)
    c: Coincident(g662,g663)
    c: Coincident(g663,g664)
    c: Coincident(g664,g665)
    c: Coincident(g665,g666)
    c: Coincident(g666,g667)
    c: Coincident(g667,g668)
    c: Coincident(g668,g669)
    c: Coincident(g669,g670)
    c: Coincident(g670,g671)
    c: Coincident(g671,g672)
    c: Coincident(g672,g673)
    c: Horizontal(g673)
    c: Coincident(g673,g674)
    c: Coincident(g674,g675)
    c: Coincident(g675,g676)
    c: Coincident(g676,g677)
    c: Coincident(g677,g678)
    c: Vertical(g678)
    c: Coincident(g678,g679)
    c: Coincident(g680,g681)
    c: Vertical(g681)
    c: Coincident(g681,g682)
    c: Horizontal(g682)
    c: Coincident(g682,g683)
    c: Coincident(g683,g684)
    c: Coincident(g684,g685)
    c: Coincident(g685,g686)
    c: Coincident(g686,g687)
    c: Vertical(g687)
    c: Coincident(g687,g688)
    c: Coincident(g688,g689)
    c: Coincident(g689,g690)
    c: Coincident(g690,g691)
    c: Coincident(g691,g692)
    c: Coincident(g692,g693)
    c: Coincident(g693,g694)
    c: Horizontal(g694)
    c: Coincident(g694,g695)
    c: Horizontal(g508)
    c: Vertical(g509)
    c: Horizontal(g510)
    c: Vertical(g519)
    c: Vertical(g517)
    c: Horizontal(g520)
    c: Coincident(g520,g696)
    c: Coincident(g696,g697)
    c: Horizontal(g697)
    c: Coincident(g697,g698)
    c: Coincident(g698,g521)
    c: Vertical(g698)
    c: Vertical(g522)
    c: Vertical(g524)
    c: Vertical(g526)
    c: Horizontal(g523)
    c: Horizontal(g525)
    c: Horizontal(g527)
    c: Horizontal(g529)
    c: Horizontal(g532)
    c: Horizontal(g521)
    c: Vertical(g528)
    c: Vertical(g530)
    c: Coincident(g530,g699)
    c: Coincident(g699,g700)
    c: Coincident(g700,g701)
    c: Coincident(g701,g531)
    c: Vertical(g700)
    c: Vertical(g531)
    c: Vertical(g533)
    c: Vertical(g535)
    c: Vertical(g537)
    c: Vertical(g539)
    c: Vertical(g541)
    c: Horizontal(g534)
    c: Horizontal(g536)
    c: Horizontal(g538)
    c: Horizontal(g540)
    c: Horizontal(g542)
    c: Horizontal(g544)
    c: Horizontal(g546)
    c: Horizontal(g699)
    c: Horizontal(g701)
    c: Vertical(g543)
    c: Vertical(g545)
    c: Vertical(g547)
    c: Vertical(g549)
    c: Horizontal(g548)
    c: Vertical(g555)
    c: Vertical(g553)
    c: Vertical(g551)
    c: Horizontal(g552)
    c: Horizontal(g556)
    c: Horizontal(g560)
    c: Vertical(g557)
    c: Vertical(g559)
    c: Vertical(g561)
    c: Coincident(g702,g562)
    c: Coincident(g702,g561)
    c: Horizontal(g565)
    c: Horizontal(g569)
    c: Horizontal(g571)
    c: Horizontal(g573)
    c: Horizontal(g575)
    c: Horizontal(g702)
    c: Vertical(g566)
    c: Vertical(g568)
    c: Vertical(g570)
    c: Vertical(g572)
    c: Vertical(g574)
    c: Vertical(g576)
    c: Vertical(g578)
    c: Vertical(g582)
    c: Vertical(g584)
    c: Horizontal(g577)
    c: Horizontal(g579)
    c: Horizontal(g581)
    c: Horizontal(g583)
    c: Horizontal(g587)
    c: Horizontal(g589)
    c: Horizontal(g591)
    c: Coincident(g591,g592)
    c: Vertical(g590)
    c: Vertical(g592)
    c: Vertical(g594)
    c: Vertical(g602)
    c: Vertical(g604)
    c: Horizontal(g595)
    c: Horizontal(g599)
    c: Horizontal(g605)
    c: Horizontal(g607)
    c: Vertical(g608)
    c: Vertical(g611)
    c: Horizontal(g612)
    c: Horizontal(g614)
    c: Horizontal(g620)
    c: Horizontal(g622)
    c: Vertical(g621)
    c: Vertical(g623)
    c: Coincident(g618,g703)
    c: Vertical(g703)
    c: Coincident(g703,g704)
    c: Horizontal(g704)
    c: Coincident(g704,g617)
    c: Horizontal(g624)
    c: Vertical(g625)
    c: Horizontal(g643)
    c: Horizontal(g645)
    c: Horizontal(g647)
    c: Horizontal(g649)
    c: Horizontal(g651)
    c: Horizontal(g653)
    c: Horizontal(g655)
    c: Horizontal(g657)
    c: Horizontal(g659)
    c: Vertical(g656)
    c: Vertical(g654)
    c: Vertical(g650)
    c: Vertical(g648)
    c: Vertical(g646)
    c: Vertical(g637)
    c: Vertical(g639)
    c: Horizontal(g661)
    c: Horizontal(g663)
    c: Horizontal(g665)
    c: Horizontal(g667)
    c: Horizontal(g669)
    c: Horizontal(g671)
    c: Horizontal(g675)
    c: Vertical(g662)
    c: Vertical(g664)
    c: Vertical(g666)
    c: Vertical(g668)
    c: Vertical(g670)
    c: Vertical(g672)
    c: Vertical(g674)
    c: Vertical(g676)
    c: Horizontal(g677)
    c: Horizontal(g679)
    c: Coincident(g679,g705)
    c: Vertical(g705)
    c: Coincident(g705,g706)
    c: Horizontal(g706)
    c: Coincident(g706,g707)
    c: Coincident(g680,g707)
    c: Horizontal(g680)
    c: Vertical(g707)
    c: Vertical(g691)
    c: Vertical(g693)
    c: Vertical(g689)
    c: Vertical(g685)
    c: Vertical(g683)
    c: Horizontal(g686)
    c: Horizontal(g688)
    c: Horizontal(g690)
    c: Horizontal(g692)
    c: Horizontal(g684)
    c: Vertical(g695)
    c: Coincident(g695,g708)
    c: Coincident(g708,g709)
    c: Coincident(g709,g710)
    c: Coincident(g710,g711)
    c: Coincident(g711,g712)
    c: Coincident(g712,g713)
    c: Horizontal(g713)
    c: Coincident(g713,g714)
    c: Coincident(g714,g715)
    c: Coincident(g715,g716)
    c: Coincident(g716,g717)
    c: Coincident(g718,g719)
    c: Horizontal(g720)
    c: Coincident(g721,g722)
    c: Coincident(g722,g723)
    c: Coincident(g723,g724)
    c: Horizontal(g724)
    c: Coincident(g724,g725)
    c: Horizontal(g726)
    c: Coincident(g726,g727)
    c: Coincident(g727,g728)
    c: Horizontal(g728)
    c: Coincident(g728,g729)
    c: Coincident(g729,g730)
    c: Coincident(g730,g731)
    c: Coincident(g731,g732)
    c: Coincident(g732,g733)
    c: Coincident(g733,g734)
    c: Coincident(g734,g735)
    c: Coincident(g735,g736)
    c: Coincident(g736,g737)
    c: Coincident(g737,g738)
    c: Coincident(g738,g739)
    c: Coincident(g739,g740)
    c: Coincident(g740,g741)
    c: Coincident(g741,g742)
    c: Coincident(g742,g743)
    c: Coincident(g743,g744)
    c: Coincident(g744,g745)
    c: Coincident(g745,g746)
    c: Coincident(g746,g747)
    c: Coincident(g747,g748)
    c: Coincident(g748,g749)
    c: Coincident(g749,g750)
    c: Coincident(g750,g751)
    c: Coincident(g751,g752)
    c: Coincident(g752,g753)
    c: Coincident(g753,g754)
    c: Coincident(g754,g755)
    c: Coincident(g755,g756)
    c: Coincident(g756,g757)
    c: Coincident(g757,g758)
    c: Coincident(g760,g761)
    c: Coincident(g761,g762)
    c: Coincident(g762,g763)
    c: Coincident(g763,g764)
    c: Coincident(g765,g766)
    c: Coincident(g766,g767)
    c: Coincident(g767,g768)
    c: Coincident(g769,g770)
    c: Coincident(g770,g771)
    c: Coincident(g772,g773)
    c: Coincident(g773,g774)
    c: Coincident(g774,g775)
    c: Coincident(g775,g776)
    c: Coincident(g776,g777)
    c: Coincident(g777,g778)
    c: Coincident(g778,g779)
    c: Coincident(g779,g780)
    c: Coincident(g780,g781)
    c: Coincident(g781,g782)
    c: Coincident(g782,g783)
    c: Coincident(g783,g784)
    c: Coincident(g784,g785)
    c: Coincident(g785,g786)
    c: Horizontal(g787)
    c: Coincident(g787,g788)
    c: Coincident(g788,g789)
    c: Coincident(g789,g790)
    c: Coincident(g790,g791)
    c: Horizontal(g791)
    c: Coincident(g791,g792)
    c: Coincident(g792,g793)
    c: Horizontal(g793)
    c: Coincident(g793,g794)
    c: Coincident(g794,g795)
    c: Coincident(g795,g796)
    c: Vertical(g796)
    c: Coincident(g796,g797)
    c: Horizontal(g797)
    c: Coincident(g797,g798)
    c: Coincident(g798,g799)
    c: Horizontal(g799)
    c: Coincident(g799,g800)
    c: Coincident(g800,g801)
    c: Coincident(g801,g802)
    c: Coincident(g802,g803)
    c: Horizontal(g803)
    c: Vertical(g804)
    c: Coincident(g804,g805)
    c: Coincident(g805,g806)
    c: Coincident(g806,g807)
    c: Coincident(g807,g808)
    c: Coincident(g808,g809)
    c: Coincident(g809,g810)
    c: Vertical(g810)
    c: Coincident(g810,g811)
    c: Coincident(g811,g812)
    c: Coincident(g812,g813)
    c: Coincident(g813,g814)
    c: Coincident(g814,g815)
    c: Horizontal(g815)
    c: Coincident(g815,g816)
    c: Coincident(g816,g817)
    c: Coincident(g817,g818)
    c: Coincident(g818,g819)
    c: Coincident(g819,g820)
    c: Coincident(g820,g821)
    c: Horizontal(g821)
    c: Coincident(g821,g822)
    c: Vertical(g822)
    c: Coincident(g822,g823)
    c: Coincident(g823,g824)
    c: Coincident(g824,g825)
    c: Horizontal(g825)
    c: Coincident(g825,g826)
    c: Coincident(g826,g827)
    c: Coincident(g827,g828)
    c: Coincident(g828,g829)
    c: Horizontal(g829)
    c: Coincident(g829,g830)
    c: Coincident(g830,g831)
    c: Coincident(g831,g832)
    c: Coincident(g832,g833)
    c: Horizontal(g834)
    c: Coincident(g834,g835)
    c: Coincident(g835,g836)
    c: Horizontal(g836)
    c: Coincident(g836,g837)
    c: Coincident(g837,g838)
    c: Horizontal(g838)
    c: Coincident(g838,g839)
    c: Coincident(g839,g840)
    c: Coincident(g840,g841)
    c: Coincident(g841,g842)
    c: Coincident(g842,g843)
    c: Coincident(g843,g844)
    c: Coincident(g844,g845)
    c: Coincident(g845,g846)
    c: Coincident(g846,g847)
    c: Coincident(g847,g848)
    c: Horizontal(g848)
    c: Coincident(g848,g849)
    c: Coincident(g849,g850)
    c: Coincident(g850,g851)
    c: Coincident(g851,g852)
    c: Coincident(g852,g853)
    c: Coincident(g853,g854)
    c: Coincident(g854,g855)
    c: Coincident(g855,g856)
    c: Coincident(g856,g857)
    c: Coincident(g857,g858)
    c: Horizontal(g858)
    c: Coincident(g858,g859)
    c: Coincident(g859,g860)
    c: Coincident(g860,g861)
    c: Coincident(g861,g862)
    c: Coincident(g862,g863)
    c: Coincident(g863,g864)
    c: Coincident(g786,g865)
    c: Coincident(g865,g866)
    c: Coincident(g866,g787)
    c: Vertical(g866)
    c: Horizontal(g709)
    c: Horizontal(g711)
    c: Horizontal(g715)
    c: Horizontal(g717)
    c: Horizontal(g719)
    c: Horizontal(g722)
    c: Coincident(g718,g867)
    c: Horizontal(g867)
    c: Coincident(g867,g868)
    c: Coincident(g868,g717)
    c: Coincident(g721,g869)
    c: Coincident(g869,g870)
    c: Coincident(g720,g870)
    c: Coincident(g871,g720)
    c: Coincident(g871,g719)
    c: Vertical(g871)
    c: Vertical(g870)
    c: Vertical(g723)
    c: Horizontal(g869)
    c: Coincident(g872,g726)
    c: Coincident(g873,g872)
    c: Coincident(g725,g873)
    c: Horizontal(g873)
    c: Horizontal(g736)
    c: Horizontal(g734)
    c: Horizontal(g732)
    c: Horizontal(g730)
    c: Horizontal(g738)
    c: Horizontal(g740)
    c: Horizontal(g742)
    c: Horizontal(g744)
    c: Horizontal(g746)
    c: Horizontal(g748)
    c: Horizontal(g750)
    c: Horizontal(g752)
    c: Horizontal(g754)
    c: Coincident(g758,g759)
    c: Horizontal(g756)
    c: Horizontal(g758)
    c: Coincident(g874,g759)
    c: Horizontal(g874)
    c: Coincident(g875,g760)
    c: Coincident(g875,g874)
    c: Horizontal(g760)
    c: Vertical(g762)
    c: Coincident(g765,g764)
    c: Vertical(g764)
    c: Vertical(g766)
    c: Vertical(g768)
    c: Coincident(g769,g768)
    c: Vertical(g770)
    c: Coincident(g876,g771)
    c: Coincident(g877,g772)
    c: Coincident(g877,g876)
    c: Vertical(g772)
    c: Vertical(g774)
    c: Vertical(g776)
    c: Vertical(g778)
    c: Vertical(g780)
    c: Vertical(g782)
    c: Vertical(g876)
    c: Horizontal(g773)
    c: Horizontal(g775)
    c: Horizontal(g777)
    c: Horizontal(g779)
    c: Horizontal(g781)
    c: Horizontal(g783)
    c: Horizontal(g785)
    c: Horizontal(g865)
    c: Vertical(g784)
    c: Vertical(g786)
    c: Vertical(g788)
    c: Vertical(g790)
    c: Horizontal(g789)
    c: Vertical(g792)
    c: Vertical(g794)
    c: Horizontal(g795)
    c: Vertical(g798)
    c: Vertical(g800)
    c: Vertical(g802)
    c: Horizontal(g801)
    c: Coincident(g804,g803)
    c: Horizontal(g805)
    c: Horizontal(g807)
    c: Horizontal(g809)
    c: Vertical(g806)
    c: Vertical(g808)
    c: Vertical(g812)
    c: Vertical(g816)
    c: Vertical(g814)
    c: Vertical(g818)
    c: Vertical(g820)
    c: Vertical(g824)
    c: Vertical(g826)
    c: Vertical(g828)
    c: Vertical(g830)
    c: Vertical(g832)
    c: Horizontal(g827)
    c: Horizontal(g823)
    c: Horizontal(g819)
    c: Horizontal(g817)
    c: Horizontal(g831)
    c: Horizontal(g833)
    c: Coincident(g878,g833)
    c: Coincident(g878,g834)
    c: Vertical(g837)
    c: Horizontal(g840)
    c: Horizontal(g842)
    c: Horizontal(g846)
    c: Horizontal(g850)
    c: Horizontal(g852)
    c: Horizontal(g854)
    c: Horizontal(g856)
    c: Horizontal(g860)
    c: Horizontal(g862)
    c: Horizontal(g864)
    c: Horizontal(g844)
    c: Coincident(g864,g879)
    c: Coincident(g879,g880)
    c: Coincident(g880,g881)
    c: Coincident(g881,g882)
    c: Horizontal(g882)
    c: Coincident(g883,g1)
    c: Coincident(g883,g0)
    c: Vertical(g883)
    c: Coincident(g0,g882)
    c: Coincident(g1,g2)
    c: Coincident(g3,g4)
    c: Coincident(g4,g5)
    c: Coincident(g5,g6)
    c: Coincident(g6,g7)
    c: Coincident(g13,g14)
    c: Coincident(g14,g15)
    c: Coincident(g16,g17)
    c: Coincident(g18,g19)
    c: Coincident(g22,g23)
    c: Coincident(g24,g25)
    c: Coincident(g27,g28)
    c: Vertical(g26)
    c: Coincident(g28,g29)
    c: Coincident(g30,g31)
    c: Horizontal(g29)
    c: Coincident(g37,g38)
    c: Coincident(g38,g39)
    c: Coincident(g39,g40)
    c: Coincident(g40,g41)
    c: Coincident(g42,g43)
    c: Coincident(g20,g21)
    c: Coincident(g21,g22)
    c: Coincident(g25,g26)
    c: Coincident(g48,g49)
    c: Coincident(g49,g50)
    c: Coincident(g58,g59)
    c: Horizontal(g59)
    c: Coincident(g61,g62)
    c: Coincident(g64,g65)
    c: Coincident(g65,g66)
    c: Coincident(g66,g67)
    c: Coincident(g68,g69)
    c: Coincident(g70,g71)
    c: Coincident(g72,g73)
    c: Coincident(g74,g75)
    c: Coincident(g86,g87)
    c: Coincident(g87,g88)
    c: Coincident(g92,g93)
    c: Coincident(g94,g95)
    c: Coincident(g96,g97)
    c: Coincident(g51,g52)
    c: Coincident(g62,g63)
    c: Coincident(g76,g77)
    c: Coincident(g77,g78)
    c: Coincident(g82,g83)
    c: Coincident(g83,g84)
FEATURE [Part::Extrusion] Extrude001  label="logo002"
  Base = -> Sketch013
  Dir = (0,1,0)
  DirMode = 0
  FaceMakerClass = Part::FaceMakerBullseye
  LengthFwd = 10
  LengthRev = 0
  Solid = true
  Symmetric = false
FEATURE [Mesh::Feature] tinker  label="logo001"
  Placement = pos=(42,-32.19,20) rot=(1,0,0;1.5708rad)
